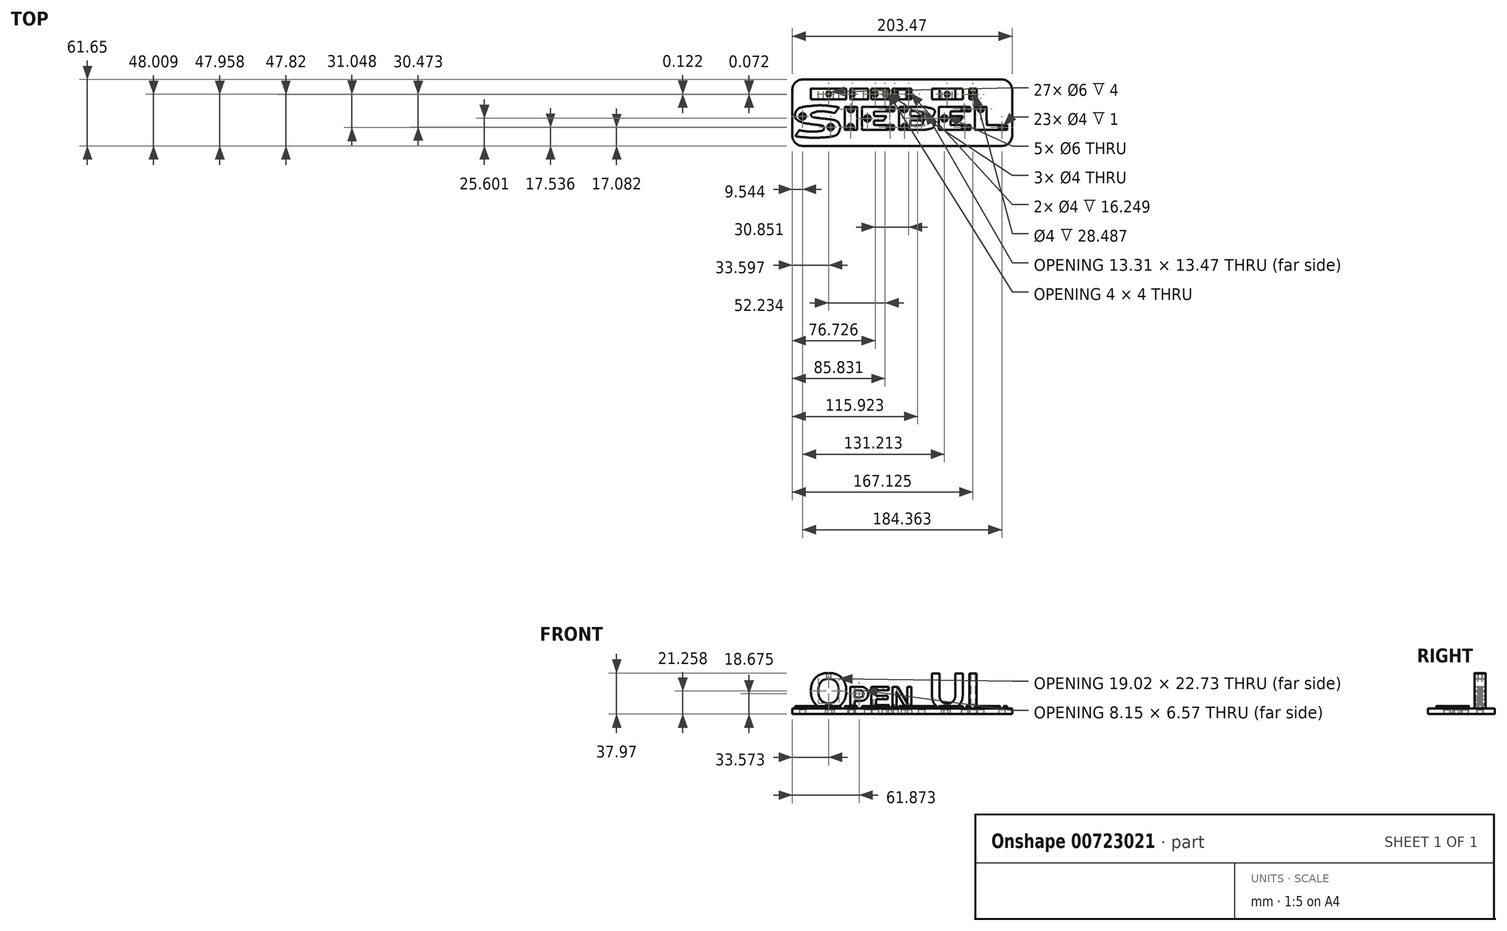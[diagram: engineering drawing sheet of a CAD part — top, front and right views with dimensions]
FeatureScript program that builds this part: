
annotation { "Feature Type Name" : "Feature", "Feature Type Description" : "" }
export const myFeature = defineFeature(function(context is Context, id is Id, definition is map)
    precondition{}
    {
        {
            var Q0;
            Q0=qCreatedBy(makeId("Top.planeOp"),FACE);
            var sketch = newSketch(context, id + "F0", { "sketchPlane" : qUnion([Q0])});
            skFitSpline(sketch, "E0", {"points": [v(-354.96, -59.06) * mm, v(-378.2, -57.21) * mm, v(-400.75, -54.4) * mm, v(-402.03, -53.2) * mm]});
            skFitSpline(sketch, "E1", {"points": [v(-402.03, -53.2) * mm, v(-402.4, -52.85) * mm, v(-399.54, -47.84) * mm, v(-395.68, -42.05) * mm]});
            skFitSpline(sketch, "E2", {"points": [v(-395.68, -42.05) * mm, v(-389.24, -32.38) * mm, v(-388.5, -31.56) * mm, v(-386.61, -31.95) * mm]});
            skFitSpline(sketch, "E3", {"points": [v(-386.61, -31.95) * mm, v(-370.93, -35.2) * mm, v(-331.08, -37.36) * mm, v(-318.28, -35.65) * mm]});
            skFitSpline(sketch, "E4", {"points": [v(-318.28, -35.65) * mm, v(-305.45, -33.93) * mm, v(-298.56, -29.94) * mm, v(-298.56, -24.22) * mm]});
            skFitSpline(sketch, "E5", {"points": [v(-298.56, -24.22) * mm, v(-298.56, -18.07) * mm, v(-306.97, -14.43) * mm, v(-327.76, -11.58) * mm]});
            skFitSpline(sketch, "E6", {"points": [v(-327.76, -11.58) * mm, v(-362.95, -6.76) * mm, v(-372.07, -5.05) * mm, v(-381.63, -1.45) * mm]});
            skFitSpline(sketch, "E7", {"points": [v(-381.63, -1.45) * mm, v(-389.44, 1.49) * mm, v(-392.84, 3.44) * mm, v(-397.15, 7.47) * mm]});
            skFitSpline(sketch, "E8", {"points": [v(-397.15, 7.47) * mm, v(-402.93, 12.88) * mm, v(-404.52, 16.34) * mm, v(-404.54, 23.62) * mm]});
            skFitSpline(sketch, "E9", {"points": [v(-404.54, 23.62) * mm, v(-404.56, 28.77) * mm, v(-404.24, 30.16) * mm, v(-402.32, 33.43) * mm]});
            skFitSpline(sketch, "E10", {"points": [v(-402.32, 33.43) * mm, v(-395.06, 45.78) * mm, v(-371.6, 54.87) * mm, v(-337.66, 58.48) * mm]});
            skFitSpline(sketch, "E11", {"points": [v(-337.66, 58.48) * mm, v(-322.85, 60.05) * mm, v(-292.3, 59.65) * mm, v(-275.36, 57.66) * mm]});
            skFitSpline(sketch, "E12", {"points": [v(-275.36, 57.66) * mm, v(-262.37, 56.14) * mm, v(-244.13, 53.26) * mm, v(-242.8, 52.53) * mm]});
            skFitSpline(sketch, "E13", {"points": [v(-242.8, 52.53) * mm, v(-242.17, 52.18) * mm, v(-244.56, 48.55) * mm, v(-249.77, 41.96) * mm]});
            skFitSpline(sketch, "E14", {"points": [v(-266.73, 33.28) * mm, v(-294.41, 37.46) * mm, v(-321.46, 37.5) * mm, v(-334.5, 33.4) * mm]});
            skFitSpline(sketch, "E15", {"points": [v(-334.5, 33.4) * mm, v(-342.06, 31.02) * mm, v(-345.84, 25.86) * mm, v(-343.4, 21.28) * mm]});
            skFitSpline(sketch, "E16", {"points": [v(-343.4, 21.28) * mm, v(-341.53, 17.8) * mm, v(-331.4, 15.1) * mm, v(-310.06, 12.42) * mm]});
            skFitSpline(sketch, "E17", {"points": [v(-310.06, 12.42) * mm, v(-266.73, 6.98) * mm, v(-246.51, -0.28) * mm, v(-239.92, -12.73) * mm]});
            skFitSpline(sketch, "E18", {"points": [v(-239.92, -12.73) * mm, v(-237.55, -17.2) * mm, v(-237.58, -25.67) * mm, v(-239.99, -31.03) * mm]});
            skFitSpline(sketch, "E19", {"points": [v(-239.99, -31.03) * mm, v(-246.48, -45.5) * mm, v(-271.26, -55.64) * mm, v(-307.76, -58.75) * mm]});
            skFitSpline(sketch, "E20", {"points": [v(-307.76, -58.75) * mm, v(-316.45, -59.49) * mm, v(-347.03, -59.7) * mm, v(-354.96, -59.06) * mm]});
            skLineSegment(sketch, "E21", {"start": v(-249.77, 41.96) * mm, "end": v(-257.7, 31.91) * mm});
            skLineSegment(sketch, "E22", {"start": v(-257.7, 31.91) * mm, "end": v(-266.73, 33.28) * mm});
            skLineSegment(sketch, "E23", {"start": v(-220.96, 12.02) * mm, "end": v(-220.96, 54.82) * mm});
            skLineSegment(sketch, "E24", {"start": v(-220.96, 54.82) * mm, "end": v(-197.76, 54.82) * mm});
            skLineSegment(sketch, "E25", {"start": v(-197.76, 54.82) * mm, "end": v(-174.56, 54.82) * mm});
            skLineSegment(sketch, "E26", {"start": v(-174.56, 54.82) * mm, "end": v(-174.56, 12.02) * mm});
            skLineSegment(sketch, "E27", {"start": v(-174.56, 12.02) * mm, "end": v(-174.56, -30.78) * mm});
            skLineSegment(sketch, "E28", {"start": v(-174.56, -30.78) * mm, "end": v(-197.76, -30.78) * mm});
            skLineSegment(sketch, "E29", {"start": v(-197.76, -30.78) * mm, "end": v(-220.96, -30.78) * mm});
            skLineSegment(sketch, "E30", {"start": v(-220.96, -30.78) * mm, "end": v(-220.96, 12.02) * mm});
            skFitSpline(sketch, "E31", {"points": [v(-20.16, 1.76) * mm, v(-20.16, 19.72) * mm, v(-19.92, 39) * mm, v(-19.63, 44.62) * mm]});
            skLineSegment(sketch, "E32", {"start": v(-156.96, 12.02) * mm, "end": v(-156.96, 54.82) * mm});
            skLineSegment(sketch, "E33", {"start": v(-156.96, 54.82) * mm, "end": v(-96.93, 54.82) * mm});
            skLineSegment(sketch, "E34", {"start": v(-96.93, 54.82) * mm, "end": v(-36.9, 54.82) * mm});
            skLineSegment(sketch, "E35", {"start": v(-36.9, 54.82) * mm, "end": v(-37.13, 46.22) * mm});
            skLineSegment(sketch, "E36", {"start": v(-37.13, 46.22) * mm, "end": v(-37.36, 37.62) * mm});
            skLineSegment(sketch, "E37", {"start": v(-37.36, 37.62) * mm, "end": v(-74.79, 37.4) * mm});
            skLineSegment(sketch, "E38", {"start": v(-74.79, 37.4) * mm, "end": v(-112.22, 37.2) * mm});
            skLineSegment(sketch, "E39", {"start": v(-112.22, 37.2) * mm, "end": v(-111.99, 29) * mm});
            skLineSegment(sketch, "E40", {"start": v(-111.99, 29) * mm, "end": v(-111.76, 20.82) * mm});
            skLineSegment(sketch, "E41", {"start": v(-111.76, 20.82) * mm, "end": v(-89.19, 20.42) * mm});
            skLineSegment(sketch, "E42", {"start": v(-89.19, 20.42) * mm, "end": v(-66.62, 20.02) * mm});
            skLineSegment(sketch, "E43", {"start": v(-66.62, 20.02) * mm, "end": v(-71.86, 11.82) * mm});
            skLineSegment(sketch, "E44", {"start": v(-71.86, 11.82) * mm, "end": v(-77.1, 3.62) * mm});
            skLineSegment(sketch, "E45", {"start": v(-77.1, 3.62) * mm, "end": v(-94.63, 3.62) * mm});
            skLineSegment(sketch, "E46", {"start": v(-94.63, 3.62) * mm, "end": v(-112.16, 3.62) * mm});
            skLineSegment(sketch, "E47", {"start": v(-112.16, 3.62) * mm, "end": v(-112.16, -4.78) * mm});
            skLineSegment(sketch, "E48", {"start": v(-112.16, -4.78) * mm, "end": v(-112.16, -13.18) * mm});
            skLineSegment(sketch, "E49", {"start": v(-112.16, -13.18) * mm, "end": v(-75.36, -13.18) * mm});
            skLineSegment(sketch, "E50", {"start": v(-75.36, -13.18) * mm, "end": v(-38.56, -13.18) * mm});
            skLineSegment(sketch, "E51", {"start": v(-38.56, -13.18) * mm, "end": v(-38.56, -21.98) * mm});
            skLineSegment(sketch, "E52", {"start": v(-38.56, -21.98) * mm, "end": v(-38.56, -30.78) * mm});
            skLineSegment(sketch, "E53", {"start": v(-38.56, -30.78) * mm, "end": v(-97.76, -30.78) * mm});
            skLineSegment(sketch, "E54", {"start": v(-97.76, -30.78) * mm, "end": v(-156.96, -30.78) * mm});
            skLineSegment(sketch, "E55", {"start": v(-156.96, -30.78) * mm, "end": v(-156.96, 12.02) * mm});
            skFitSpline(sketch, "E56", {"points": [v(24.16, 54.8) * mm, v(68.81, 54.78) * mm, v(77.5, 54.3) * mm, v(89.34, 51.24) * mm]});
            skFitSpline(sketch, "E57", {"points": [v(89.34, 51.24) * mm, v(105.78, 46.98) * mm, v(113.7, 38.02) * mm, v(109.88, 28.02) * mm]});
            skFitSpline(sketch, "E58", {"points": [v(109.88, 28.02) * mm, v(107.47, 21.7) * mm, v(100.41, 17.1) * mm, v(88.56, 14.12) * mm]});
            skFitSpline(sketch, "E59", {"points": [v(88.56, 14.12) * mm, v(83.93, 12.95) * mm, v(83.08, 12.52) * mm, v(84.64, 12.17) * mm]});
            skFitSpline(sketch, "E60", {"points": [v(84.64, 12.17) * mm, v(95.63, 9.67) * mm, v(98.47, 8.79) * mm, v(102.58, 6.57) * mm]});
            skFitSpline(sketch, "E61", {"points": [v(102.58, 6.57) * mm, v(109.46, 2.87) * mm, v(112.1, -0.78) * mm, v(112.44, -7.01) * mm]});
            skFitSpline(sketch, "E62", {"points": [v(112.44, -7.01) * mm, v(112.66, -11.07) * mm, v(112.37, -12.57) * mm, v(110.86, -15.16) * mm]});
            skFitSpline(sketch, "E63", {"points": [v(110.86, -15.16) * mm, v(107.2, -21.45) * mm, v(98.2, -25.98) * mm, v(83.44, -28.93) * mm]});
            skFitSpline(sketch, "E64", {"points": [v(83.44, -28.93) * mm, v(78.12, -30) * mm, v(68.82, -30.27) * mm, v(28.44, -30.55) * mm]});
            skLineSegment(sketch, "E65", {"start": v(-19.63, 44.62) * mm, "end": v(-19.11, 54.82) * mm});
            skLineSegment(sketch, "E66", {"start": v(-19.11, 54.82) * mm, "end": v(24.16, 54.8) * mm});
            skFitSpline(sketch, "E67", {"points": [v(62.24, -12.7) * mm, v(66.78, -10.61) * mm, v(68.16, -8.94) * mm, v(68.16, -5.53) * mm]});
            skFitSpline(sketch, "E68", {"points": [v(68.16, -5.53) * mm, v(68.16, -2.08) * mm, v(65.6, 0.7) * mm, v(60.74, 2.52) * mm]});
            skFitSpline(sketch, "E69", {"points": [v(60.74, 2.52) * mm, v(57.78, 3.63) * mm, v(53.58, 3.96) * mm, v(39.64, 4.23) * mm]});
            skLineSegment(sketch, "E70", {"start": v(28.44, -30.55) * mm, "end": v(-20.16, -30.9) * mm});
            skLineSegment(sketch, "E71", {"start": v(-20.16, -30.9) * mm, "end": v(-20.16, 1.76) * mm});
            skLineSegment(sketch, "E72", {"start": v(-20.16, 1.76) * mm, "end": v(-20.16, 1.76) * mm});
            skFitSpline(sketch, "E73", {"points": [v(40.44, -14.64) * mm, v(56.77, -14.38) * mm, v(59.01, -14.18) * mm, v(62.24, -12.7) * mm]});
            skLineSegment(sketch, "E74", {"start": v(39.64, 4.23) * mm, "end": v(22.24, 4.55) * mm});
            skLineSegment(sketch, "E75", {"start": v(22.24, 4.55) * mm, "end": v(22.24, -5.2) * mm});
            skLineSegment(sketch, "E76", {"start": v(22.24, -5.2) * mm, "end": v(22.24, -14.94) * mm});
            skLineSegment(sketch, "E77", {"start": v(22.24, -14.94) * mm, "end": v(40.44, -14.64) * mm});
            skFitSpline(sketch, "E78", {"points": [v(55.04, 21.27) * mm, v(57.9, 21.74) * mm, v(61.67, 22.9) * mm, v(63.42, 23.87) * mm]});
            skFitSpline(sketch, "E79", {"points": [v(63.42, 23.87) * mm, v(69.57, 27.26) * mm, v(69.07, 33.28) * mm, v(62.36, 36.59) * mm]});
            skFitSpline(sketch, "E80", {"points": [v(62.36, 36.59) * mm, v(58.87, 38.3) * mm, v(57.5, 38.43) * mm, v(40.44, 38.68) * mm]});
            skFitSpline(sketch, "E81", {"points": [v(36.04, 20.42) * mm, v(43.63, 20.43) * mm, v(52.18, 20.8) * mm, v(55.04, 21.27) * mm]});
            skLineSegment(sketch, "E82", {"start": v(40.44, 38.68) * mm, "end": v(22.24, 38.95) * mm});
            skLineSegment(sketch, "E83", {"start": v(22.24, 38.95) * mm, "end": v(22.24, 29.68) * mm});
            skLineSegment(sketch, "E84", {"start": v(22.24, 29.68) * mm, "end": v(22.24, 20.42) * mm});
            skLineSegment(sketch, "E85", {"start": v(22.24, 20.42) * mm, "end": v(36.04, 20.42) * mm});
            skLineSegment(sketch, "E86", {"start": v(55.04, 21.27) * mm, "end": v(55.04, 21.27) * mm});
            skFitSpline(sketch, "E87", {"points": [v(243.32, 48.7) * mm, v(243.6, 45.33) * mm, v(243.84, 41.55) * mm, v(243.84, 40.3) * mm]});
            skLineSegment(sketch, "E88", {"start": v(127.04, 12.02) * mm, "end": v(127.04, 54.82) * mm});
            skLineSegment(sketch, "E89", {"start": v(127.04, 54.82) * mm, "end": v(184.92, 54.82) * mm});
            skLineSegment(sketch, "E90", {"start": v(184.92, 54.82) * mm, "end": v(242.8, 54.82) * mm});
            skLineSegment(sketch, "E91", {"start": v(242.8, 54.82) * mm, "end": v(243.32, 48.7) * mm});
            skLineSegment(sketch, "E92", {"start": v(243.84, 40.3) * mm, "end": v(243.84, 38.02) * mm});
            skLineSegment(sketch, "E93", {"start": v(243.84, 38.02) * mm, "end": v(207.44, 38.02) * mm});
            skLineSegment(sketch, "E94", {"start": v(207.44, 38.02) * mm, "end": v(171.04, 38.02) * mm});
            skLineSegment(sketch, "E95", {"start": v(171.04, 38.02) * mm, "end": v(171.04, 29.23) * mm});
            skLineSegment(sketch, "E96", {"start": v(171.04, 29.23) * mm, "end": v(171.04, 20.44) * mm});
            skLineSegment(sketch, "E97", {"start": v(171.04, 20.44) * mm, "end": v(193.73, 20.23) * mm});
            skLineSegment(sketch, "E98", {"start": v(193.73, 20.23) * mm, "end": v(216.43, 20.02) * mm});
            skLineSegment(sketch, "E99", {"start": v(216.43, 20.02) * mm, "end": v(211.18, 11.82) * mm});
            skLineSegment(sketch, "E100", {"start": v(211.18, 11.82) * mm, "end": v(205.94, 3.62) * mm});
            skLineSegment(sketch, "E101", {"start": v(205.94, 3.62) * mm, "end": v(188.49, 3.62) * mm});
            skLineSegment(sketch, "E102", {"start": v(188.49, 3.62) * mm, "end": v(171.04, 3.62) * mm});
            skLineSegment(sketch, "E103", {"start": v(171.04, 3.62) * mm, "end": v(171.04, -4.78) * mm});
            skLineSegment(sketch, "E104", {"start": v(171.04, -4.78) * mm, "end": v(171.04, -13.18) * mm});
            skLineSegment(sketch, "E105", {"start": v(171.04, -13.18) * mm, "end": v(207.44, -13.18) * mm});
            skLineSegment(sketch, "E106", {"start": v(207.44, -13.18) * mm, "end": v(243.84, -13.18) * mm});
            skLineSegment(sketch, "E107", {"start": v(243.84, -13.18) * mm, "end": v(243.84, -21.98) * mm});
            skLineSegment(sketch, "E108", {"start": v(243.84, -21.98) * mm, "end": v(243.84, -30.78) * mm});
            skLineSegment(sketch, "E109", {"start": v(243.84, -30.78) * mm, "end": v(185.44, -30.78) * mm});
            skLineSegment(sketch, "E110", {"start": v(185.44, -30.78) * mm, "end": v(127.04, -30.78) * mm});
            skLineSegment(sketch, "E111", {"start": v(127.04, -30.78) * mm, "end": v(127.04, 12.02) * mm});
            skFitSpline(sketch, "E112", {"points": [v(304.64, 30.22) * mm, v(304.65, 16.69) * mm, v(304.88, 1.57) * mm, v(305.17, -3.38) * mm]});
            skLineSegment(sketch, "E113", {"start": v(260.64, 12.02) * mm, "end": v(260.64, 54.82) * mm});
            skLineSegment(sketch, "E114", {"start": v(260.64, 54.82) * mm, "end": v(282.64, 54.82) * mm});
            skLineSegment(sketch, "E115", {"start": v(282.64, 54.82) * mm, "end": v(304.64, 54.82) * mm});
            skLineSegment(sketch, "E116", {"start": v(304.64, 54.82) * mm, "end": v(304.64, 30.22) * mm});
            skLineSegment(sketch, "E117", {"start": v(305.17, -3.38) * mm, "end": v(305.68, -12.38) * mm});
            skLineSegment(sketch, "E118", {"start": v(305.68, -12.38) * mm, "end": v(343.16, -12.38) * mm});
            skLineSegment(sketch, "E119", {"start": v(343.16, -12.38) * mm, "end": v(380.64, -12.38) * mm});
            skLineSegment(sketch, "E120", {"start": v(380.64, -12.38) * mm, "end": v(380.64, -21.58) * mm});
            skLineSegment(sketch, "E121", {"start": v(380.64, -21.58) * mm, "end": v(380.64, -30.78) * mm});
            skLineSegment(sketch, "E122", {"start": v(380.64, -30.78) * mm, "end": v(320.64, -30.78) * mm});
            skLineSegment(sketch, "E123", {"start": v(320.64, -30.78) * mm, "end": v(260.64, -30.78) * mm});
            skLineSegment(sketch, "E124", {"start": v(260.64, -30.78) * mm, "end": v(260.64, 12.02) * mm});
            skSolve(sketch);
        }
        {
            var Q0;
            Q0=makeQuery(id+"F0.imprint","IMPRINT",FACE,{"disambiguationData":[TD([[makeQuery(id+"F0.imprint","IMPRINT",EDGE,{"derivedFrom":sQuery(id+"F0.wireOp",EDGE,"E0")}),-1.0]])]});
            var Q1;
            Q1=makeQuery(id+"F0.imprint","IMPRINT",FACE,{"disambiguationData":[TD([[makeQuery(id+"F0.imprint","IMPRINT",EDGE,{"derivedFrom":sQuery(id+"F0.wireOp",EDGE,"E23")}),-1.0]])]});
            var Q2;
            Q2=makeQuery(id+"F0.imprint","IMPRINT",FACE,{"disambiguationData":[TD([[makeQuery(id+"F0.imprint","IMPRINT",EDGE,{"derivedFrom":sQuery(id+"F0.wireOp",EDGE,"E32")}),-1.0]])]});
            var Q3;
            Q3=makeQuery(id+"F0.imprint","IMPRINT",FACE,{"disambiguationData":[TD([[makeQuery(id+"F0.imprint","IMPRINT",EDGE,{"derivedFrom":sQuery(id+"F0.wireOp",EDGE,"E31")}),-1.0]])]});
            var Q4;
            Q4=makeQuery(id+"F0.imprint","IMPRINT",FACE,{"disambiguationData":[TD([[makeQuery(id+"F0.imprint","IMPRINT",EDGE,{"derivedFrom":sQuery(id+"F0.wireOp",EDGE,"E87")}),-1.0]])]});
            var Q5;
            Q5=makeQuery(id+"F0.imprint","IMPRINT",FACE,{"disambiguationData":[TD([[makeQuery(id+"F0.imprint","IMPRINT",EDGE,{"derivedFrom":sQuery(id+"F0.wireOp",EDGE,"E112")}),-1.0]])]});
            extrude(context, id + "F1", {"entities" : qUnion([Q0, Q1, Q2, Q3, Q4, Q5]), "depth" : 10 * mm, "offsetDistance" : 25 * mm});
        }
        {
            var Q0;
            Q0=qCreatedBy(makeId("Front.planeOp"),FACE);
            var sketch = newSketch(context, id + "F2", { "sketchPlane" : qUnion([Q0])});
            skText(sketch, "E125", { "text": "UI", "fontName": "Arimo-Bold.ttf"});
            skText(sketch, "E126", { "text": "O", "fontName": "Arimo-Bold.ttf"});
            skText(sketch, "E127", { "text": "PEN", "fontName": "Arimo-Bold.ttf"});
            const initialGuessF2  = {"E125": [-0.03631, 0, 1, 0, 0.085], "E126": [-0.31434, 0, 1, 0, 0.085], "E127": [-0.22355, 0, 1, 0, 0.05298]};
            skSetInitialGuess(sketch, initialGuessF2);
            skSolve(sketch);
        }
        {
            var Q0;
            Q0 = qSketchRegion(id + "F2", true);
            extrude(context, id + "F3", {"entities" : qUnion([Q0]), "depth" : 25 * mm, "offsetDistance" : 25 * mm});
        }
        {
            var Q0;
            Q0=makeQuery(id+"F3.opExtrude","SWEPT_BODY",BODY,{"disambiguationData":[OSD([sQuery(id+"F2.wireOp",EDGE,"E127.sketch_text.stroke-28"),sQuery(id+"F2.wireOp",EDGE,"E127.sketch_text.stroke-29"),sQuery(id+"F2.wireOp",EDGE,"E127.sketch_text.stroke-30"),sQuery(id+"F2.wireOp",EDGE,"E127.sketch_text.stroke-31"),sQuery(id+"F2.wireOp",EDGE,"E127.sketch_text.stroke-32"),sQuery(id+"F2.wireOp",EDGE,"E127.sketch_text.stroke-33"),sQuery(id+"F2.wireOp",EDGE,"E127.sketch_text.stroke-34"),sQuery(id+"F2.wireOp",EDGE,"E127.sketch_text.stroke-35"),sQuery(id+"F2.wireOp",EDGE,"E127.sketch_text.stroke-36"),sQuery(id+"F2.wireOp",EDGE,"E127.sketch_text.stroke-37"),sQuery(id+"F2.wireOp",EDGE,"E127.sketch_text.stroke-38"),sQuery(id+"F2.wireOp",EDGE,"E127.sketch_text.stroke-39")])]});
            var Q1;
            Q1=makeQuery(id+"F3.opExtrude","SWEPT_BODY",BODY,{"disambiguationData":[OSD([sQuery(id+"F2.wireOp",EDGE,"E127.sketch_text.stroke-16"),sQuery(id+"F2.wireOp",EDGE,"E127.sketch_text.stroke-17"),sQuery(id+"F2.wireOp",EDGE,"E127.sketch_text.stroke-18"),sQuery(id+"F2.wireOp",EDGE,"E127.sketch_text.stroke-19"),sQuery(id+"F2.wireOp",EDGE,"E127.sketch_text.stroke-20"),sQuery(id+"F2.wireOp",EDGE,"E127.sketch_text.stroke-21"),sQuery(id+"F2.wireOp",EDGE,"E127.sketch_text.stroke-22"),sQuery(id+"F2.wireOp",EDGE,"E127.sketch_text.stroke-23"),sQuery(id+"F2.wireOp",EDGE,"E127.sketch_text.stroke-24"),sQuery(id+"F2.wireOp",EDGE,"E127.sketch_text.stroke-25"),sQuery(id+"F2.wireOp",EDGE,"E127.sketch_text.stroke-26"),sQuery(id+"F2.wireOp",EDGE,"E127.sketch_text.stroke-27")])]});
            var Q2;
            Q2=makeQuery(id+"F3.opExtrude","SWEPT_BODY",BODY,{"disambiguationData":[OSD([sQuery(id+"F2.wireOp",EDGE,"E127.sketch_text.stroke-0"),sQuery(id+"F2.wireOp",EDGE,"E127.sketch_text.stroke-1"),sQuery(id+"F2.wireOp",EDGE,"E127.sketch_text.stroke-2"),sQuery(id+"F2.wireOp",EDGE,"E127.sketch_text.stroke-3"),sQuery(id+"F2.wireOp",EDGE,"E127.sketch_text.stroke-4"),sQuery(id+"F2.wireOp",EDGE,"E127.sketch_text.stroke-5"),sQuery(id+"F2.wireOp",EDGE,"E127.sketch_text.stroke-6"),sQuery(id+"F2.wireOp",EDGE,"E127.sketch_text.stroke-7"),sQuery(id+"F2.wireOp",EDGE,"E127.sketch_text.stroke-8"),sQuery(id+"F2.wireOp",EDGE,"E127.sketch_text.stroke-9"),sQuery(id+"F2.wireOp",EDGE,"E127.sketch_text.stroke-10"),sQuery(id+"F2.wireOp",EDGE,"E127.sketch_text.stroke-11"),sQuery(id+"F2.wireOp",EDGE,"E127.sketch_text.stroke-12"),sQuery(id+"F2.wireOp",EDGE,"E127.sketch_text.stroke-13"),sQuery(id+"F2.wireOp",EDGE,"E127.sketch_text.stroke-14"),sQuery(id+"F2.wireOp",EDGE,"E127.sketch_text.stroke-15")])]});
            var Q3;
            Q3=makeQuery(id+"F3.opExtrude","SWEPT_BODY",BODY,{"disambiguationData":[OSD([sQuery(id+"F2.wireOp",EDGE,"E126.sketch_text.stroke-0"),sQuery(id+"F2.wireOp",EDGE,"E126.sketch_text.stroke-1"),sQuery(id+"F2.wireOp",EDGE,"E126.sketch_text.stroke-2"),sQuery(id+"F2.wireOp",EDGE,"E126.sketch_text.stroke-3"),sQuery(id+"F2.wireOp",EDGE,"E126.sketch_text.stroke-4"),sQuery(id+"F2.wireOp",EDGE,"E126.sketch_text.stroke-5"),sQuery(id+"F2.wireOp",EDGE,"E126.sketch_text.stroke-6"),sQuery(id+"F2.wireOp",EDGE,"E126.sketch_text.stroke-7"),sQuery(id+"F2.wireOp",EDGE,"E126.sketch_text.stroke-8"),sQuery(id+"F2.wireOp",EDGE,"E126.sketch_text.stroke-9"),sQuery(id+"F2.wireOp",EDGE,"E126.sketch_text.stroke-10"),sQuery(id+"F2.wireOp",EDGE,"E126.sketch_text.stroke-11"),sQuery(id+"F2.wireOp",EDGE,"E126.sketch_text.stroke-12"),sQuery(id+"F2.wireOp",EDGE,"E126.sketch_text.stroke-13"),sQuery(id+"F2.wireOp",EDGE,"E126.sketch_text.stroke-14"),sQuery(id+"F2.wireOp",EDGE,"E126.sketch_text.stroke-15"),sQuery(id+"F2.wireOp",EDGE,"E126.sketch_text.stroke-16")])]});
            var Q4;
            Q4=makeQuery(id+"F3.opExtrude","SWEPT_BODY",BODY,{"disambiguationData":[OSD([sQuery(id+"F2.wireOp",EDGE,"E125.sketch_text.stroke-14"),sQuery(id+"F2.wireOp",EDGE,"E125.sketch_text.stroke-15"),sQuery(id+"F2.wireOp",EDGE,"E125.sketch_text.stroke-16"),sQuery(id+"F2.wireOp",EDGE,"E125.sketch_text.stroke-17")])]});
            var Q5;
            Q5=makeQuery(id+"F3.opExtrude","SWEPT_BODY",BODY,{"disambiguationData":[OSD([sQuery(id+"F2.wireOp",EDGE,"E125.sketch_text.stroke-0"),sQuery(id+"F2.wireOp",EDGE,"E125.sketch_text.stroke-1"),sQuery(id+"F2.wireOp",EDGE,"E125.sketch_text.stroke-2"),sQuery(id+"F2.wireOp",EDGE,"E125.sketch_text.stroke-3"),sQuery(id+"F2.wireOp",EDGE,"E125.sketch_text.stroke-4"),sQuery(id+"F2.wireOp",EDGE,"E125.sketch_text.stroke-5"),sQuery(id+"F2.wireOp",EDGE,"E125.sketch_text.stroke-6"),sQuery(id+"F2.wireOp",EDGE,"E125.sketch_text.stroke-7"),sQuery(id+"F2.wireOp",EDGE,"E125.sketch_text.stroke-8"),sQuery(id+"F2.wireOp",EDGE,"E125.sketch_text.stroke-9"),sQuery(id+"F2.wireOp",EDGE,"E125.sketch_text.stroke-10"),sQuery(id+"F2.wireOp",EDGE,"E125.sketch_text.stroke-11"),sQuery(id+"F2.wireOp",EDGE,"E125.sketch_text.stroke-12"),sQuery(id+"F2.wireOp",EDGE,"E125.sketch_text.stroke-13")])]});
            transform(context, id + "F4", {"entities" : qUnion([Q0, Q1, Q2, Q3, Q4, Q5]), "transformType" : TransformType.TRANSLATION_3D, "dx" : 0 * mm, "dy" : 107 * mm, "dz" : 0 * mm, "makeCopy" : false});
        }
        {
            var Q0;
            Q0=makeQuery(id+"F1.opExtrude","SWEPT_BODY",BODY,{"disambiguationData":[OSD([sQuery(id+"F0.wireOp",EDGE,"E0"),sQuery(id+"F0.wireOp",EDGE,"E1"),sQuery(id+"F0.wireOp",EDGE,"E2"),sQuery(id+"F0.wireOp",EDGE,"E3"),sQuery(id+"F0.wireOp",EDGE,"E4"),sQuery(id+"F0.wireOp",EDGE,"E5"),sQuery(id+"F0.wireOp",EDGE,"E6"),sQuery(id+"F0.wireOp",EDGE,"E7"),sQuery(id+"F0.wireOp",EDGE,"E8"),sQuery(id+"F0.wireOp",EDGE,"E9"),sQuery(id+"F0.wireOp",EDGE,"E10"),sQuery(id+"F0.wireOp",EDGE,"E11"),sQuery(id+"F0.wireOp",EDGE,"E12"),sQuery(id+"F0.wireOp",EDGE,"E13"),sQuery(id+"F0.wireOp",EDGE,"E14"),sQuery(id+"F0.wireOp",EDGE,"E15"),sQuery(id+"F0.wireOp",EDGE,"E16"),sQuery(id+"F0.wireOp",EDGE,"E17"),sQuery(id+"F0.wireOp",EDGE,"E18"),sQuery(id+"F0.wireOp",EDGE,"E19"),sQuery(id+"F0.wireOp",EDGE,"E20"),sQuery(id+"F0.wireOp",EDGE,"E21"),sQuery(id+"F0.wireOp",EDGE,"E22")])]});
            var Q1;
            Q1=makeQuery(id+"F1.opExtrude","SWEPT_BODY",BODY,{"disambiguationData":[OSD([sQuery(id+"F0.wireOp",EDGE,"E112"),sQuery(id+"F0.wireOp",EDGE,"E113"),sQuery(id+"F0.wireOp",EDGE,"E114"),sQuery(id+"F0.wireOp",EDGE,"E115"),sQuery(id+"F0.wireOp",EDGE,"E116"),sQuery(id+"F0.wireOp",EDGE,"E117"),sQuery(id+"F0.wireOp",EDGE,"E118"),sQuery(id+"F0.wireOp",EDGE,"E119"),sQuery(id+"F0.wireOp",EDGE,"E120"),sQuery(id+"F0.wireOp",EDGE,"E121"),sQuery(id+"F0.wireOp",EDGE,"E122"),sQuery(id+"F0.wireOp",EDGE,"E123"),sQuery(id+"F0.wireOp",EDGE,"E124")])]});
            var Q2;
            Q2=makeQuery(id+"F1.opExtrude","SWEPT_BODY",BODY,{"disambiguationData":[OSD([sQuery(id+"F0.wireOp",EDGE,"E23"),sQuery(id+"F0.wireOp",EDGE,"E24"),sQuery(id+"F0.wireOp",EDGE,"E25"),sQuery(id+"F0.wireOp",EDGE,"E26"),sQuery(id+"F0.wireOp",EDGE,"E27"),sQuery(id+"F0.wireOp",EDGE,"E28"),sQuery(id+"F0.wireOp",EDGE,"E29"),sQuery(id+"F0.wireOp",EDGE,"E30")])]});
            var Q3;
            Q3=makeQuery(id+"F1.opExtrude","SWEPT_BODY",BODY,{"disambiguationData":[OSD([sQuery(id+"F0.wireOp",EDGE,"E31"),sQuery(id+"F0.wireOp",EDGE,"E56"),sQuery(id+"F0.wireOp",EDGE,"E57"),sQuery(id+"F0.wireOp",EDGE,"E58"),sQuery(id+"F0.wireOp",EDGE,"E59"),sQuery(id+"F0.wireOp",EDGE,"E60"),sQuery(id+"F0.wireOp",EDGE,"E61"),sQuery(id+"F0.wireOp",EDGE,"E62"),sQuery(id+"F0.wireOp",EDGE,"E63"),sQuery(id+"F0.wireOp",EDGE,"E64"),sQuery(id+"F0.wireOp",EDGE,"E65"),sQuery(id+"F0.wireOp",EDGE,"E66"),sQuery(id+"F0.wireOp",EDGE,"E67"),sQuery(id+"F0.wireOp",EDGE,"E68"),sQuery(id+"F0.wireOp",EDGE,"E69"),sQuery(id+"F0.wireOp",EDGE,"E70"),sQuery(id+"F0.wireOp",EDGE,"E71"),sQuery(id+"F0.wireOp",EDGE,"E73"),sQuery(id+"F0.wireOp",EDGE,"E74"),sQuery(id+"F0.wireOp",EDGE,"E75"),sQuery(id+"F0.wireOp",EDGE,"E76"),sQuery(id+"F0.wireOp",EDGE,"E77"),sQuery(id+"F0.wireOp",EDGE,"E78"),sQuery(id+"F0.wireOp",EDGE,"E79"),sQuery(id+"F0.wireOp",EDGE,"E80"),sQuery(id+"F0.wireOp",EDGE,"E81"),sQuery(id+"F0.wireOp",EDGE,"E82"),sQuery(id+"F0.wireOp",EDGE,"E83"),sQuery(id+"F0.wireOp",EDGE,"E84"),sQuery(id+"F0.wireOp",EDGE,"E85"),sQuery(id+"F0.wireOp",EDGE,"E86")])]});
            var Q4;
            Q4=makeQuery(id+"F1.opExtrude","SWEPT_BODY",BODY,{"disambiguationData":[OSD([sQuery(id+"F0.wireOp",EDGE,"E32"),sQuery(id+"F0.wireOp",EDGE,"E33"),sQuery(id+"F0.wireOp",EDGE,"E34"),sQuery(id+"F0.wireOp",EDGE,"E35"),sQuery(id+"F0.wireOp",EDGE,"E36"),sQuery(id+"F0.wireOp",EDGE,"E37"),sQuery(id+"F0.wireOp",EDGE,"E38"),sQuery(id+"F0.wireOp",EDGE,"E39"),sQuery(id+"F0.wireOp",EDGE,"E40"),sQuery(id+"F0.wireOp",EDGE,"E41"),sQuery(id+"F0.wireOp",EDGE,"E42"),sQuery(id+"F0.wireOp",EDGE,"E43"),sQuery(id+"F0.wireOp",EDGE,"E44"),sQuery(id+"F0.wireOp",EDGE,"E45"),sQuery(id+"F0.wireOp",EDGE,"E46"),sQuery(id+"F0.wireOp",EDGE,"E47"),sQuery(id+"F0.wireOp",EDGE,"E48"),sQuery(id+"F0.wireOp",EDGE,"E49"),sQuery(id+"F0.wireOp",EDGE,"E50"),sQuery(id+"F0.wireOp",EDGE,"E51"),sQuery(id+"F0.wireOp",EDGE,"E52"),sQuery(id+"F0.wireOp",EDGE,"E53"),sQuery(id+"F0.wireOp",EDGE,"E54"),sQuery(id+"F0.wireOp",EDGE,"E55")])]});
            var Q5;
            Q5=makeQuery(id+"F1.opExtrude","SWEPT_BODY",BODY,{"disambiguationData":[OSD([sQuery(id+"F0.wireOp",EDGE,"E87"),sQuery(id+"F0.wireOp",EDGE,"E88"),sQuery(id+"F0.wireOp",EDGE,"E89"),sQuery(id+"F0.wireOp",EDGE,"E90"),sQuery(id+"F0.wireOp",EDGE,"E91"),sQuery(id+"F0.wireOp",EDGE,"E92"),sQuery(id+"F0.wireOp",EDGE,"E93"),sQuery(id+"F0.wireOp",EDGE,"E94"),sQuery(id+"F0.wireOp",EDGE,"E95"),sQuery(id+"F0.wireOp",EDGE,"E96"),sQuery(id+"F0.wireOp",EDGE,"E97"),sQuery(id+"F0.wireOp",EDGE,"E98"),sQuery(id+"F0.wireOp",EDGE,"E99"),sQuery(id+"F0.wireOp",EDGE,"E100"),sQuery(id+"F0.wireOp",EDGE,"E101"),sQuery(id+"F0.wireOp",EDGE,"E102"),sQuery(id+"F0.wireOp",EDGE,"E103"),sQuery(id+"F0.wireOp",EDGE,"E104"),sQuery(id+"F0.wireOp",EDGE,"E105"),sQuery(id+"F0.wireOp",EDGE,"E106"),sQuery(id+"F0.wireOp",EDGE,"E107"),sQuery(id+"F0.wireOp",EDGE,"E108"),sQuery(id+"F0.wireOp",EDGE,"E109"),sQuery(id+"F0.wireOp",EDGE,"E110"),sQuery(id+"F0.wireOp",EDGE,"E111")])]});
            var Q6;
            Q6=qCreatedBy(makeId("Origin.pointOp"),VERTEX);
            transform(context, id + "F5", {"entities" : qUnion([Q0, Q1, Q2, Q3, Q4, Q5]), "transformType" : TransformType.SCALE_UNIFORMLY, "scale" : 0.25, "scalePoint" : qUnion([Q6]), "makeCopy" : false});
        }
        {
            var Q0;
            Q0=makeQuery(id+"F3.opExtrude","SWEPT_BODY",BODY,{"disambiguationData":[OSD([sQuery(id+"F2.wireOp",EDGE,"E125.sketch_text.stroke-0"),sQuery(id+"F2.wireOp",EDGE,"E125.sketch_text.stroke-1"),sQuery(id+"F2.wireOp",EDGE,"E125.sketch_text.stroke-2"),sQuery(id+"F2.wireOp",EDGE,"E125.sketch_text.stroke-3"),sQuery(id+"F2.wireOp",EDGE,"E125.sketch_text.stroke-4"),sQuery(id+"F2.wireOp",EDGE,"E125.sketch_text.stroke-5"),sQuery(id+"F2.wireOp",EDGE,"E125.sketch_text.stroke-6"),sQuery(id+"F2.wireOp",EDGE,"E125.sketch_text.stroke-7"),sQuery(id+"F2.wireOp",EDGE,"E125.sketch_text.stroke-8"),sQuery(id+"F2.wireOp",EDGE,"E125.sketch_text.stroke-9"),sQuery(id+"F2.wireOp",EDGE,"E125.sketch_text.stroke-10"),sQuery(id+"F2.wireOp",EDGE,"E125.sketch_text.stroke-11"),sQuery(id+"F2.wireOp",EDGE,"E125.sketch_text.stroke-12"),sQuery(id+"F2.wireOp",EDGE,"E125.sketch_text.stroke-13")])]});
            var Q1;
            Q1=makeQuery(id+"F3.opExtrude","SWEPT_BODY",BODY,{"disambiguationData":[OSD([sQuery(id+"F2.wireOp",EDGE,"E125.sketch_text.stroke-14"),sQuery(id+"F2.wireOp",EDGE,"E125.sketch_text.stroke-15"),sQuery(id+"F2.wireOp",EDGE,"E125.sketch_text.stroke-16"),sQuery(id+"F2.wireOp",EDGE,"E125.sketch_text.stroke-17")])]});
            var Q2;
            Q2=makeQuery(id+"F3.opExtrude","SWEPT_BODY",BODY,{"disambiguationData":[OSD([sQuery(id+"F2.wireOp",EDGE,"E126.sketch_text.stroke-0"),sQuery(id+"F2.wireOp",EDGE,"E126.sketch_text.stroke-1"),sQuery(id+"F2.wireOp",EDGE,"E126.sketch_text.stroke-2"),sQuery(id+"F2.wireOp",EDGE,"E126.sketch_text.stroke-3"),sQuery(id+"F2.wireOp",EDGE,"E126.sketch_text.stroke-4"),sQuery(id+"F2.wireOp",EDGE,"E126.sketch_text.stroke-5"),sQuery(id+"F2.wireOp",EDGE,"E126.sketch_text.stroke-6"),sQuery(id+"F2.wireOp",EDGE,"E126.sketch_text.stroke-7"),sQuery(id+"F2.wireOp",EDGE,"E126.sketch_text.stroke-8"),sQuery(id+"F2.wireOp",EDGE,"E126.sketch_text.stroke-9"),sQuery(id+"F2.wireOp",EDGE,"E126.sketch_text.stroke-10"),sQuery(id+"F2.wireOp",EDGE,"E126.sketch_text.stroke-11"),sQuery(id+"F2.wireOp",EDGE,"E126.sketch_text.stroke-12"),sQuery(id+"F2.wireOp",EDGE,"E126.sketch_text.stroke-13"),sQuery(id+"F2.wireOp",EDGE,"E126.sketch_text.stroke-14"),sQuery(id+"F2.wireOp",EDGE,"E126.sketch_text.stroke-15"),sQuery(id+"F2.wireOp",EDGE,"E126.sketch_text.stroke-16")])]});
            var Q3;
            Q3=makeQuery(id+"F3.opExtrude","SWEPT_BODY",BODY,{"disambiguationData":[OSD([sQuery(id+"F2.wireOp",EDGE,"E127.sketch_text.stroke-0"),sQuery(id+"F2.wireOp",EDGE,"E127.sketch_text.stroke-1"),sQuery(id+"F2.wireOp",EDGE,"E127.sketch_text.stroke-2"),sQuery(id+"F2.wireOp",EDGE,"E127.sketch_text.stroke-3"),sQuery(id+"F2.wireOp",EDGE,"E127.sketch_text.stroke-4"),sQuery(id+"F2.wireOp",EDGE,"E127.sketch_text.stroke-5"),sQuery(id+"F2.wireOp",EDGE,"E127.sketch_text.stroke-6"),sQuery(id+"F2.wireOp",EDGE,"E127.sketch_text.stroke-7"),sQuery(id+"F2.wireOp",EDGE,"E127.sketch_text.stroke-8"),sQuery(id+"F2.wireOp",EDGE,"E127.sketch_text.stroke-9"),sQuery(id+"F2.wireOp",EDGE,"E127.sketch_text.stroke-10"),sQuery(id+"F2.wireOp",EDGE,"E127.sketch_text.stroke-11"),sQuery(id+"F2.wireOp",EDGE,"E127.sketch_text.stroke-12"),sQuery(id+"F2.wireOp",EDGE,"E127.sketch_text.stroke-13"),sQuery(id+"F2.wireOp",EDGE,"E127.sketch_text.stroke-14"),sQuery(id+"F2.wireOp",EDGE,"E127.sketch_text.stroke-15")])]});
            var Q4;
            Q4=makeQuery(id+"F3.opExtrude","SWEPT_BODY",BODY,{"disambiguationData":[OSD([sQuery(id+"F2.wireOp",EDGE,"E127.sketch_text.stroke-16"),sQuery(id+"F2.wireOp",EDGE,"E127.sketch_text.stroke-17"),sQuery(id+"F2.wireOp",EDGE,"E127.sketch_text.stroke-18"),sQuery(id+"F2.wireOp",EDGE,"E127.sketch_text.stroke-19"),sQuery(id+"F2.wireOp",EDGE,"E127.sketch_text.stroke-20"),sQuery(id+"F2.wireOp",EDGE,"E127.sketch_text.stroke-21"),sQuery(id+"F2.wireOp",EDGE,"E127.sketch_text.stroke-22"),sQuery(id+"F2.wireOp",EDGE,"E127.sketch_text.stroke-23"),sQuery(id+"F2.wireOp",EDGE,"E127.sketch_text.stroke-24"),sQuery(id+"F2.wireOp",EDGE,"E127.sketch_text.stroke-25"),sQuery(id+"F2.wireOp",EDGE,"E127.sketch_text.stroke-26"),sQuery(id+"F2.wireOp",EDGE,"E127.sketch_text.stroke-27")])]});
            var Q5;
            Q5=makeQuery(id+"F3.opExtrude","SWEPT_BODY",BODY,{"disambiguationData":[OSD([sQuery(id+"F2.wireOp",EDGE,"E127.sketch_text.stroke-28"),sQuery(id+"F2.wireOp",EDGE,"E127.sketch_text.stroke-29"),sQuery(id+"F2.wireOp",EDGE,"E127.sketch_text.stroke-30"),sQuery(id+"F2.wireOp",EDGE,"E127.sketch_text.stroke-31"),sQuery(id+"F2.wireOp",EDGE,"E127.sketch_text.stroke-32"),sQuery(id+"F2.wireOp",EDGE,"E127.sketch_text.stroke-33"),sQuery(id+"F2.wireOp",EDGE,"E127.sketch_text.stroke-34"),sQuery(id+"F2.wireOp",EDGE,"E127.sketch_text.stroke-35"),sQuery(id+"F2.wireOp",EDGE,"E127.sketch_text.stroke-36"),sQuery(id+"F2.wireOp",EDGE,"E127.sketch_text.stroke-37"),sQuery(id+"F2.wireOp",EDGE,"E127.sketch_text.stroke-38"),sQuery(id+"F2.wireOp",EDGE,"E127.sketch_text.stroke-39")])]});
            var Q6;
            Q6=qCreatedBy(makeId("Origin.pointOp"),VERTEX);
            transform(context, id + "F6", {"entities" : qUnion([Q0, Q1, Q2, Q3, Q4, Q5]), "transformType" : TransformType.SCALE_UNIFORMLY, "scale" : 0.4, "scalePoint" : qUnion([Q6]), "makeCopy" : false});
        }
        {
            var Q0;
            Q0=makeQuery(id+"F3.opExtrude","SWEPT_BODY",BODY,{"disambiguationData":[OSD([sQuery(id+"F2.wireOp",EDGE,"E125.sketch_text.stroke-0"),sQuery(id+"F2.wireOp",EDGE,"E125.sketch_text.stroke-1"),sQuery(id+"F2.wireOp",EDGE,"E125.sketch_text.stroke-2"),sQuery(id+"F2.wireOp",EDGE,"E125.sketch_text.stroke-3"),sQuery(id+"F2.wireOp",EDGE,"E125.sketch_text.stroke-4"),sQuery(id+"F2.wireOp",EDGE,"E125.sketch_text.stroke-5"),sQuery(id+"F2.wireOp",EDGE,"E125.sketch_text.stroke-6"),sQuery(id+"F2.wireOp",EDGE,"E125.sketch_text.stroke-7"),sQuery(id+"F2.wireOp",EDGE,"E125.sketch_text.stroke-8"),sQuery(id+"F2.wireOp",EDGE,"E125.sketch_text.stroke-9"),sQuery(id+"F2.wireOp",EDGE,"E125.sketch_text.stroke-10"),sQuery(id+"F2.wireOp",EDGE,"E125.sketch_text.stroke-11"),sQuery(id+"F2.wireOp",EDGE,"E125.sketch_text.stroke-12"),sQuery(id+"F2.wireOp",EDGE,"E125.sketch_text.stroke-13")])]});
            var Q1;
            Q1=makeQuery(id+"F3.opExtrude","SWEPT_BODY",BODY,{"disambiguationData":[OSD([sQuery(id+"F2.wireOp",EDGE,"E125.sketch_text.stroke-14"),sQuery(id+"F2.wireOp",EDGE,"E125.sketch_text.stroke-15"),sQuery(id+"F2.wireOp",EDGE,"E125.sketch_text.stroke-16"),sQuery(id+"F2.wireOp",EDGE,"E125.sketch_text.stroke-17")])]});
            var Q2;
            Q2=makeQuery(id+"F3.opExtrude","SWEPT_BODY",BODY,{"disambiguationData":[OSD([sQuery(id+"F2.wireOp",EDGE,"E126.sketch_text.stroke-0"),sQuery(id+"F2.wireOp",EDGE,"E126.sketch_text.stroke-1"),sQuery(id+"F2.wireOp",EDGE,"E126.sketch_text.stroke-2"),sQuery(id+"F2.wireOp",EDGE,"E126.sketch_text.stroke-3"),sQuery(id+"F2.wireOp",EDGE,"E126.sketch_text.stroke-4"),sQuery(id+"F2.wireOp",EDGE,"E126.sketch_text.stroke-5"),sQuery(id+"F2.wireOp",EDGE,"E126.sketch_text.stroke-6"),sQuery(id+"F2.wireOp",EDGE,"E126.sketch_text.stroke-7"),sQuery(id+"F2.wireOp",EDGE,"E126.sketch_text.stroke-8"),sQuery(id+"F2.wireOp",EDGE,"E126.sketch_text.stroke-9"),sQuery(id+"F2.wireOp",EDGE,"E126.sketch_text.stroke-10"),sQuery(id+"F2.wireOp",EDGE,"E126.sketch_text.stroke-11"),sQuery(id+"F2.wireOp",EDGE,"E126.sketch_text.stroke-12"),sQuery(id+"F2.wireOp",EDGE,"E126.sketch_text.stroke-13"),sQuery(id+"F2.wireOp",EDGE,"E126.sketch_text.stroke-14"),sQuery(id+"F2.wireOp",EDGE,"E126.sketch_text.stroke-15"),sQuery(id+"F2.wireOp",EDGE,"E126.sketch_text.stroke-16")])]});
            var Q3;
            Q3=makeQuery(id+"F3.opExtrude","SWEPT_BODY",BODY,{"disambiguationData":[OSD([sQuery(id+"F2.wireOp",EDGE,"E127.sketch_text.stroke-0"),sQuery(id+"F2.wireOp",EDGE,"E127.sketch_text.stroke-1"),sQuery(id+"F2.wireOp",EDGE,"E127.sketch_text.stroke-2"),sQuery(id+"F2.wireOp",EDGE,"E127.sketch_text.stroke-3"),sQuery(id+"F2.wireOp",EDGE,"E127.sketch_text.stroke-4"),sQuery(id+"F2.wireOp",EDGE,"E127.sketch_text.stroke-5"),sQuery(id+"F2.wireOp",EDGE,"E127.sketch_text.stroke-6"),sQuery(id+"F2.wireOp",EDGE,"E127.sketch_text.stroke-7"),sQuery(id+"F2.wireOp",EDGE,"E127.sketch_text.stroke-8"),sQuery(id+"F2.wireOp",EDGE,"E127.sketch_text.stroke-9"),sQuery(id+"F2.wireOp",EDGE,"E127.sketch_text.stroke-10"),sQuery(id+"F2.wireOp",EDGE,"E127.sketch_text.stroke-11"),sQuery(id+"F2.wireOp",EDGE,"E127.sketch_text.stroke-12"),sQuery(id+"F2.wireOp",EDGE,"E127.sketch_text.stroke-13"),sQuery(id+"F2.wireOp",EDGE,"E127.sketch_text.stroke-14"),sQuery(id+"F2.wireOp",EDGE,"E127.sketch_text.stroke-15")])]});
            var Q4;
            Q4=makeQuery(id+"F3.opExtrude","SWEPT_BODY",BODY,{"disambiguationData":[OSD([sQuery(id+"F2.wireOp",EDGE,"E127.sketch_text.stroke-16"),sQuery(id+"F2.wireOp",EDGE,"E127.sketch_text.stroke-17"),sQuery(id+"F2.wireOp",EDGE,"E127.sketch_text.stroke-18"),sQuery(id+"F2.wireOp",EDGE,"E127.sketch_text.stroke-19"),sQuery(id+"F2.wireOp",EDGE,"E127.sketch_text.stroke-20"),sQuery(id+"F2.wireOp",EDGE,"E127.sketch_text.stroke-21"),sQuery(id+"F2.wireOp",EDGE,"E127.sketch_text.stroke-22"),sQuery(id+"F2.wireOp",EDGE,"E127.sketch_text.stroke-23"),sQuery(id+"F2.wireOp",EDGE,"E127.sketch_text.stroke-24"),sQuery(id+"F2.wireOp",EDGE,"E127.sketch_text.stroke-25"),sQuery(id+"F2.wireOp",EDGE,"E127.sketch_text.stroke-26"),sQuery(id+"F2.wireOp",EDGE,"E127.sketch_text.stroke-27")])]});
            var Q5;
            Q5=makeQuery(id+"F3.opExtrude","SWEPT_BODY",BODY,{"disambiguationData":[OSD([sQuery(id+"F2.wireOp",EDGE,"E127.sketch_text.stroke-28"),sQuery(id+"F2.wireOp",EDGE,"E127.sketch_text.stroke-29"),sQuery(id+"F2.wireOp",EDGE,"E127.sketch_text.stroke-30"),sQuery(id+"F2.wireOp",EDGE,"E127.sketch_text.stroke-31"),sQuery(id+"F2.wireOp",EDGE,"E127.sketch_text.stroke-32"),sQuery(id+"F2.wireOp",EDGE,"E127.sketch_text.stroke-33"),sQuery(id+"F2.wireOp",EDGE,"E127.sketch_text.stroke-34"),sQuery(id+"F2.wireOp",EDGE,"E127.sketch_text.stroke-35"),sQuery(id+"F2.wireOp",EDGE,"E127.sketch_text.stroke-36"),sQuery(id+"F2.wireOp",EDGE,"E127.sketch_text.stroke-37"),sQuery(id+"F2.wireOp",EDGE,"E127.sketch_text.stroke-38"),sQuery(id+"F2.wireOp",EDGE,"E127.sketch_text.stroke-39")])]});
            transform(context, id + "F7", {"entities" : qUnion([Q0, Q1, Q2, Q3, Q4, Q5]), "transformType" : TransformType.TRANSLATION_3D, "dx" : 37.3 * mm, "dy" : -12.3 * mm, "dz" : 0 * mm, "makeCopy" : false});
        }
        {
            var Q0;
            Q0=qCreatedBy(makeId("Top.planeOp"),FACE);
            var sketch = newSketch(context, id + "F8", { "sketchPlane" : qUnion([Q0])});
            skLineSegment(sketch, "E128.bottom", {"start": v(-103.71, -22.6) * mm, "end": v(99.76, -22.6) * mm});
            skLineSegment(sketch, "E128.top", {"start": v(-103.71, 39.05) * mm, "end": v(99.76, 39.05) * mm});
            skLineSegment(sketch, "E128.left", {"start": v(-103.71, -22.6) * mm, "end": v(-103.71, 39.05) * mm});
            skLineSegment(sketch, "E128.right", {"start": v(99.76, -22.6) * mm, "end": v(99.76, 39.05) * mm});
            skSolve(sketch);
        }
        {
            var Q0;
            Q0=makeQuery(id+"F8.imprint","IMPRINT",FACE,{"disambiguationData":[TD([[makeQuery(id+"F8.imprint","IMPRINT",EDGE,{"derivedFrom":sQuery(id+"F8.wireOp",EDGE,"E128.bottom")}),1.0]])]});
            extrude(context, id + "F9", {"entities" : qUnion([Q0]), "depth" : 5 * mm, "offsetDistance" : 25 * mm});
        }
        {
            var Q0;
            Q0=qCreatedBy(makeId("Top.planeOp"),FACE);
            var sketch = newSketch(context, id + "F10", { "sketchPlane" : qUnion([Q0])});
            skCircle(sketch, "E129", {"center": v(-68.08, -5.06) * mm, "radius": 3 * mm});
            skCircle(sketch, "E130", {"center": v(-94.17, 4.87) * mm, "radius": 3 * mm});
            skCircle(sketch, "E131", {"center": v(-49.72, -5.12) * mm, "radius": 3 * mm});
            skCircle(sketch, "E132", {"center": v(-49.47, 11.51) * mm, "radius": 3 * mm});
            skCircle(sketch, "E133", {"center": v(-34.14, 3) * mm, "radius": 3 * mm});
            skCircle(sketch, "E134", {"center": v(-13.3, -5.22) * mm, "radius": 3 * mm});
            skCircle(sketch, "E135", {"center": v(-13.47, 11.6) * mm, "radius": 3 * mm});
            skCircle(sketch, "E136", {"center": v(0, -5.26) * mm, "radius": 3 * mm});
            skCircle(sketch, "E137", {"center": v(0, 11.64) * mm, "radius": 3 * mm});
            skCircle(sketch, "E138", {"center": v(15.9, 2.94) * mm, "radius": 3 * mm});
            skCircle(sketch, "E139", {"center": v(55.97, -5.42) * mm, "radius": 3 * mm});
            skCircle(sketch, "E140", {"center": v(55.5, 11.78) * mm, "radius": 3 * mm});
            skCircle(sketch, "E141", {"center": v(37.05, 2.92) * mm, "radius": 3 * mm});
            skCircle(sketch, "E142", {"center": v(70.61, 11.82) * mm, "radius": 3 * mm});
            skCircle(sketch, "E143", {"center": v(90.2, -5.52) * mm, "radius": 3 * mm});
            skCircle(sketch, "E144", {"center": v(39.46, 25.28) * mm, "radius": 3 * mm});
            skCircle(sketch, "E145", {"center": v(63.42, 25.22) * mm, "radius": 3 * mm});
            skCircle(sketch, "E146", {"center": v(-9.03, 25.39) * mm, "radius": 3 * mm});
            skCircle(sketch, "E147", {"center": v(3.87, 25.36) * mm, "radius": 3 * mm});
            skCircle(sketch, "E148", {"center": v(-17.88, 25.4) * mm, "radius": 3 * mm});
            skCircle(sketch, "E149", {"center": v(-26.98, 25.43) * mm, "radius": 3 * mm});
            skCircle(sketch, "E150", {"center": v(-48.23, 25.48) * mm, "radius": 3 * mm});
            skCircle(sketch, "E151", {"center": v(-70.11, 25.53) * mm, "radius": 3 * mm});
            skCircle(sketch, "E152", {"center": v(-94.17, 4.87) * mm, "radius": 2 * mm});
            skCircle(sketch, "E153", {"center": v(-68.08, -5.06) * mm, "radius": 2 * mm});
            skCircle(sketch, "E154", {"center": v(-49.72, -5.12) * mm, "radius": 2 * mm});
            skCircle(sketch, "E155", {"center": v(-49.47, 11.51) * mm, "radius": 2 * mm});
            skCircle(sketch, "E156", {"center": v(-34.14, 3) * mm, "radius": 2 * mm});
            skCircle(sketch, "E157", {"center": v(-13.3, -5.22) * mm, "radius": 2 * mm});
            skCircle(sketch, "E158", {"center": v(-13.47, 11.6) * mm, "radius": 2 * mm});
            skCircle(sketch, "E159", {"center": v(0, 11.64) * mm, "radius": 2 * mm});
            skCircle(sketch, "E160", {"center": v(0, -5.26) * mm, "radius": 2 * mm});
            skCircle(sketch, "E161", {"center": v(15.9, 2.94) * mm, "radius": 2 * mm});
            skCircle(sketch, "E162", {"center": v(37.05, 2.92) * mm, "radius": 2 * mm});
            skCircle(sketch, "E163", {"center": v(55.97, -5.42) * mm, "radius": 2 * mm});
            skCircle(sketch, "E164", {"center": v(55.5, 11.78) * mm, "radius": 2 * mm});
            skCircle(sketch, "E165", {"center": v(70.61, 11.82) * mm, "radius": 2 * mm});
            skCircle(sketch, "E166", {"center": v(90.2, -5.52) * mm, "radius": 2 * mm});
            skCircle(sketch, "E167", {"center": v(63.42, 25.22) * mm, "radius": 2 * mm});
            skCircle(sketch, "E168", {"center": v(39.46, 25.28) * mm, "radius": 2 * mm});
            skCircle(sketch, "E169", {"center": v(3.87, 25.36) * mm, "radius": 2 * mm});
            skCircle(sketch, "E170", {"center": v(-9.03, 25.39) * mm, "radius": 2 * mm});
            skCircle(sketch, "E171", {"center": v(-17.88, 25.4) * mm, "radius": 2 * mm});
            skCircle(sketch, "E172", {"center": v(-26.98, 25.43) * mm, "radius": 2 * mm});
            skCircle(sketch, "E173", {"center": v(-48.23, 25.48) * mm, "radius": 2 * mm});
            skCircle(sketch, "E174", {"center": v(-70.11, 25.53) * mm, "radius": 2 * mm});
            skLineSegment(sketch, "E175", {"start": v(-68.08, -5.06) * mm, "end": v(-49.72, -5.12) * mm, "construction": true});
            skLineSegment(sketch, "E176", {"start": v(-49.72, -5.12) * mm, "end": v(-13.3, -5.22) * mm, "construction": true});
            skLineSegment(sketch, "E177", {"start": v(-13.3, -5.22) * mm, "end": v(0, -5.26) * mm, "construction": true});
            skLineSegment(sketch, "E178", {"start": v(0, -5.26) * mm, "end": v(55.97, -5.42) * mm, "construction": true});
            skLineSegment(sketch, "E179", {"start": v(55.97, -5.42) * mm, "end": v(90.2, -5.52) * mm, "construction": true});
            skLineSegment(sketch, "E180", {"start": v(-34.14, 3) * mm, "end": v(15.9, 2.94) * mm, "construction": true});
            skLineSegment(sketch, "E181", {"start": v(15.9, 2.94) * mm, "end": v(37.05, 2.92) * mm, "construction": true});
            skLineSegment(sketch, "E182", {"start": v(-49.47, 11.51) * mm, "end": v(-13.47, 11.6) * mm, "construction": true});
            skLineSegment(sketch, "E183", {"start": v(-13.47, 11.6) * mm, "end": v(0, 11.64) * mm, "construction": true});
            skLineSegment(sketch, "E184", {"start": v(0, 11.64) * mm, "end": v(55.5, 11.78) * mm, "construction": true});
            skLineSegment(sketch, "E185", {"start": v(55.5, 11.78) * mm, "end": v(70.61, 11.82) * mm, "construction": true});
            skLineSegment(sketch, "E186", {"start": v(-70.11, 25.53) * mm, "end": v(-48.23, 25.48) * mm, "construction": true});
            skLineSegment(sketch, "E187", {"start": v(-48.23, 25.48) * mm, "end": v(-26.98, 25.43) * mm, "construction": true});
            skLineSegment(sketch, "E188", {"start": v(-26.98, 25.43) * mm, "end": v(-17.88, 25.4) * mm, "construction": true});
            skLineSegment(sketch, "E189", {"start": v(-17.88, 25.4) * mm, "end": v(-9.03, 25.39) * mm, "construction": true});
            skLineSegment(sketch, "E190", {"start": v(-9.03, 25.39) * mm, "end": v(3.87, 25.36) * mm, "construction": true});
            skLineSegment(sketch, "E191", {"start": v(3.87, 25.36) * mm, "end": v(39.46, 25.28) * mm, "construction": true});
            skLineSegment(sketch, "E192", {"start": v(39.46, 25.28) * mm, "end": v(63.42, 25.22) * mm, "construction": true});
            skSolve(sketch);
        }
        {
            var Q0;
            Q0=makeQuery(id+"F10.imprint","IMPRINT",FACE,{"disambiguationData":[TD([[makeQuery(id+"F10.imprint","IMPRINT",EDGE,{"derivedFrom":sQuery(id+"F10.wireOp",EDGE,"E129")}),1.0]])]});
            var Q1;
            Q1=makeQuery(id+"F10.imprint","IMPRINT",FACE,{"disambiguationData":[TD([[makeQuery(id+"F10.imprint","IMPRINT",EDGE,{"derivedFrom":sQuery(id+"F10.wireOp",EDGE,"E131")}),1.0]])]});
            var Q2;
            Q2=makeQuery(id+"F10.imprint","IMPRINT",FACE,{"disambiguationData":[TD([[makeQuery(id+"F10.imprint","IMPRINT",EDGE,{"derivedFrom":sQuery(id+"F10.wireOp",EDGE,"E130")}),1.0]])]});
            var Q3;
            Q3=makeQuery(id+"F10.imprint","IMPRINT",FACE,{"disambiguationData":[TD([[makeQuery(id+"F10.imprint","IMPRINT",EDGE,{"derivedFrom":sQuery(id+"F10.wireOp",EDGE,"E132")}),1.0]])]});
            var Q4;
            Q4=makeQuery(id+"F10.imprint","IMPRINT",FACE,{"disambiguationData":[TD([[makeQuery(id+"F10.imprint","IMPRINT",EDGE,{"derivedFrom":sQuery(id+"F10.wireOp",EDGE,"E133")}),1.0]])]});
            var Q5;
            Q5=makeQuery(id+"F10.imprint","IMPRINT",FACE,{"disambiguationData":[TD([[makeQuery(id+"F10.imprint","IMPRINT",EDGE,{"derivedFrom":sQuery(id+"F10.wireOp",EDGE,"E134")}),1.0]])]});
            var Q6;
            Q6=makeQuery(id+"F10.imprint","IMPRINT",FACE,{"disambiguationData":[TD([[makeQuery(id+"F10.imprint","IMPRINT",EDGE,{"derivedFrom":sQuery(id+"F10.wireOp",EDGE,"E136")}),1.0]])]});
            var Q7;
            Q7=makeQuery(id+"F10.imprint","IMPRINT",FACE,{"disambiguationData":[TD([[makeQuery(id+"F10.imprint","IMPRINT",EDGE,{"derivedFrom":sQuery(id+"F10.wireOp",EDGE,"E138")}),1.0]])]});
            var Q8;
            Q8=makeQuery(id+"F10.imprint","IMPRINT",FACE,{"disambiguationData":[TD([[makeQuery(id+"F10.imprint","IMPRINT",EDGE,{"derivedFrom":sQuery(id+"F10.wireOp",EDGE,"E141")}),1.0]])]});
            var Q9;
            Q9=makeQuery(id+"F10.imprint","IMPRINT",FACE,{"disambiguationData":[TD([[makeQuery(id+"F10.imprint","IMPRINT",EDGE,{"derivedFrom":sQuery(id+"F10.wireOp",EDGE,"E139")}),1.0]])]});
            var Q10;
            Q10=makeQuery(id+"F10.imprint","IMPRINT",FACE,{"disambiguationData":[TD([[makeQuery(id+"F10.imprint","IMPRINT",EDGE,{"derivedFrom":sQuery(id+"F10.wireOp",EDGE,"E140")}),1.0]])]});
            var Q11;
            Q11=makeQuery(id+"F10.imprint","IMPRINT",FACE,{"disambiguationData":[TD([[makeQuery(id+"F10.imprint","IMPRINT",EDGE,{"derivedFrom":sQuery(id+"F10.wireOp",EDGE,"E142")}),1.0]])]});
            var Q12;
            Q12=makeQuery(id+"F10.imprint","IMPRINT",FACE,{"disambiguationData":[TD([[makeQuery(id+"F10.imprint","IMPRINT",EDGE,{"derivedFrom":sQuery(id+"F10.wireOp",EDGE,"E143")}),1.0]])]});
            var Q13;
            Q13=makeQuery(id+"F10.imprint","IMPRINT",FACE,{"disambiguationData":[TD([[makeQuery(id+"F10.imprint","IMPRINT",EDGE,{"derivedFrom":sQuery(id+"F10.wireOp",EDGE,"E137")}),1.0]])]});
            var Q14;
            Q14=makeQuery(id+"F10.imprint","IMPRINT",FACE,{"disambiguationData":[TD([[makeQuery(id+"F10.imprint","IMPRINT",EDGE,{"derivedFrom":sQuery(id+"F10.wireOp",EDGE,"E135")}),1.0]])]});
            var Q15;
            Q15=makeQuery(id+"F10.imprint","IMPRINT",FACE,{"disambiguationData":[TD([[makeQuery(id+"F10.imprint","IMPRINT",EDGE,{"derivedFrom":sQuery(id+"F10.wireOp",EDGE,"E150")}),1.0]])]});
            var Q16;
            Q16=makeQuery(id+"F10.imprint","IMPRINT",FACE,{"disambiguationData":[TD([[makeQuery(id+"F10.imprint","IMPRINT",EDGE,{"derivedFrom":sQuery(id+"F10.wireOp",EDGE,"E149")}),1.0]])]});
            var Q17;
            Q17=makeQuery(id+"F10.imprint","IMPRINT",FACE,{"disambiguationData":[TD([[makeQuery(id+"F10.imprint","IMPRINT",EDGE,{"derivedFrom":sQuery(id+"F10.wireOp",EDGE,"E148")}),1.0]])]});
            var Q18;
            Q18=makeQuery(id+"F10.imprint","IMPRINT",FACE,{"disambiguationData":[TD([[makeQuery(id+"F10.imprint","IMPRINT",EDGE,{"derivedFrom":sQuery(id+"F10.wireOp",EDGE,"E146")}),1.0]])]});
            var Q19;
            Q19=makeQuery(id+"F10.imprint","IMPRINT",FACE,{"disambiguationData":[TD([[makeQuery(id+"F10.imprint","IMPRINT",EDGE,{"derivedFrom":sQuery(id+"F10.wireOp",EDGE,"E147")}),1.0]])]});
            var Q20;
            Q20=makeQuery(id+"F10.imprint","IMPRINT",FACE,{"disambiguationData":[TD([[makeQuery(id+"F10.imprint","IMPRINT",EDGE,{"derivedFrom":sQuery(id+"F10.wireOp",EDGE,"E145")}),1.0]])]});
            var Q21;
            Q21=makeQuery(id+"F10.imprint","IMPRINT",FACE,{"disambiguationData":[TD([[makeQuery(id+"F10.imprint","IMPRINT",EDGE,{"derivedFrom":sQuery(id+"F10.wireOp",EDGE,"E151")}),1.0]])]});
            var Q22;
            Q22=makeQuery(id+"F10.imprint","IMPRINT",FACE,{"disambiguationData":[TD([[makeQuery(id+"F10.imprint","IMPRINT",EDGE,{"derivedFrom":sQuery(id+"F10.wireOp",EDGE,"E144")}),1.0]])]});
            extrude(context, id + "F11", {"entities" : qUnion([Q0, Q1, Q2, Q3, Q4, Q5, Q6, Q7, Q8, Q9, Q10, Q11, Q12, Q13, Q14, Q15, Q16, Q17, Q18, Q19, Q20, Q21, Q22]), "operationType" : NewBodyOperationType.REMOVE, "depth" : 4 * mm, "offsetDistance" : 25 * mm});
        }
        {
            var Q0;
            Q0=makeQuery(id+"F11.boolean.opBoolean","SPLIT",FACE,{"disambiguationData":[TD([makeQuery(id+"F11.opExtrude","SWEPT_FACE",FACE,{"disambiguationData":[OSD([sQuery(id+"F10.wireOp",EDGE,"E152")])]})])],"derivedFrom":makeQuery(id+"F9.opExtrude","CAP_FACE",FACE,{"disambiguationData":[OSD([sQuery(id+"F8.wireOp",EDGE,"E128.bottom"),sQuery(id+"F8.wireOp",EDGE,"E128.top"),sQuery(id+"F8.wireOp",EDGE,"E128.left"),sQuery(id+"F8.wireOp",EDGE,"E128.right")])],"isStart":true})});
            var Q1;
            Q1=makeQuery(id+"F11.boolean.opBoolean","SPLIT",FACE,{"disambiguationData":[TD([makeQuery(id+"F11.opExtrude","SWEPT_FACE",FACE,{"disambiguationData":[OSD([sQuery(id+"F10.wireOp",EDGE,"E153")])]})])],"derivedFrom":makeQuery(id+"F9.opExtrude","CAP_FACE",FACE,{"disambiguationData":[OSD([sQuery(id+"F8.wireOp",EDGE,"E128.bottom"),sQuery(id+"F8.wireOp",EDGE,"E128.top"),sQuery(id+"F8.wireOp",EDGE,"E128.left"),sQuery(id+"F8.wireOp",EDGE,"E128.right")])],"isStart":true})});
            var Q2;
            Q2=makeQuery(id+"F11.boolean.opBoolean","SPLIT",FACE,{"disambiguationData":[TD([makeQuery(id+"F11.opExtrude","SWEPT_FACE",FACE,{"disambiguationData":[OSD([sQuery(id+"F10.wireOp",EDGE,"E154")])]})])],"derivedFrom":makeQuery(id+"F9.opExtrude","CAP_FACE",FACE,{"disambiguationData":[OSD([sQuery(id+"F8.wireOp",EDGE,"E128.bottom"),sQuery(id+"F8.wireOp",EDGE,"E128.top"),sQuery(id+"F8.wireOp",EDGE,"E128.left"),sQuery(id+"F8.wireOp",EDGE,"E128.right")])],"isStart":true})});
            var Q3;
            Q3=makeQuery(id+"F11.boolean.opBoolean","SPLIT",FACE,{"disambiguationData":[TD([makeQuery(id+"F11.opExtrude","SWEPT_FACE",FACE,{"disambiguationData":[OSD([sQuery(id+"F10.wireOp",EDGE,"E155")])]})])],"derivedFrom":makeQuery(id+"F9.opExtrude","CAP_FACE",FACE,{"disambiguationData":[OSD([sQuery(id+"F8.wireOp",EDGE,"E128.bottom"),sQuery(id+"F8.wireOp",EDGE,"E128.top"),sQuery(id+"F8.wireOp",EDGE,"E128.left"),sQuery(id+"F8.wireOp",EDGE,"E128.right")])],"isStart":true})});
            var Q4;
            Q4=makeQuery(id+"F11.boolean.opBoolean","SPLIT",FACE,{"disambiguationData":[TD([makeQuery(id+"F11.opExtrude","SWEPT_FACE",FACE,{"disambiguationData":[OSD([sQuery(id+"F10.wireOp",EDGE,"E156")])]})])],"derivedFrom":makeQuery(id+"F9.opExtrude","CAP_FACE",FACE,{"disambiguationData":[OSD([sQuery(id+"F8.wireOp",EDGE,"E128.bottom"),sQuery(id+"F8.wireOp",EDGE,"E128.top"),sQuery(id+"F8.wireOp",EDGE,"E128.left"),sQuery(id+"F8.wireOp",EDGE,"E128.right")])],"isStart":true})});
            var Q5;
            Q5=makeQuery(id+"F11.boolean.opBoolean","SPLIT",FACE,{"disambiguationData":[TD([makeQuery(id+"F11.opExtrude","SWEPT_FACE",FACE,{"disambiguationData":[OSD([sQuery(id+"F10.wireOp",EDGE,"E157")])]})])],"derivedFrom":makeQuery(id+"F9.opExtrude","CAP_FACE",FACE,{"disambiguationData":[OSD([sQuery(id+"F8.wireOp",EDGE,"E128.bottom"),sQuery(id+"F8.wireOp",EDGE,"E128.top"),sQuery(id+"F8.wireOp",EDGE,"E128.left"),sQuery(id+"F8.wireOp",EDGE,"E128.right")])],"isStart":true})});
            var Q6;
            Q6=makeQuery(id+"F11.boolean.opBoolean","SPLIT",FACE,{"disambiguationData":[TD([makeQuery(id+"F11.opExtrude","SWEPT_FACE",FACE,{"disambiguationData":[OSD([sQuery(id+"F10.wireOp",EDGE,"E160")])]})])],"derivedFrom":makeQuery(id+"F9.opExtrude","CAP_FACE",FACE,{"disambiguationData":[OSD([sQuery(id+"F8.wireOp",EDGE,"E128.bottom"),sQuery(id+"F8.wireOp",EDGE,"E128.top"),sQuery(id+"F8.wireOp",EDGE,"E128.left"),sQuery(id+"F8.wireOp",EDGE,"E128.right")])],"isStart":true})});
            var Q7;
            Q7=makeQuery(id+"F11.boolean.opBoolean","SPLIT",FACE,{"disambiguationData":[TD([makeQuery(id+"F11.opExtrude","SWEPT_FACE",FACE,{"disambiguationData":[OSD([sQuery(id+"F10.wireOp",EDGE,"E158")])]})])],"derivedFrom":makeQuery(id+"F9.opExtrude","CAP_FACE",FACE,{"disambiguationData":[OSD([sQuery(id+"F8.wireOp",EDGE,"E128.bottom"),sQuery(id+"F8.wireOp",EDGE,"E128.top"),sQuery(id+"F8.wireOp",EDGE,"E128.left"),sQuery(id+"F8.wireOp",EDGE,"E128.right")])],"isStart":true})});
            var Q8;
            Q8=makeQuery(id+"F11.boolean.opBoolean","SPLIT",FACE,{"disambiguationData":[TD([makeQuery(id+"F11.opExtrude","SWEPT_FACE",FACE,{"disambiguationData":[OSD([sQuery(id+"F10.wireOp",EDGE,"E159")])]})])],"derivedFrom":makeQuery(id+"F9.opExtrude","CAP_FACE",FACE,{"disambiguationData":[OSD([sQuery(id+"F8.wireOp",EDGE,"E128.bottom"),sQuery(id+"F8.wireOp",EDGE,"E128.top"),sQuery(id+"F8.wireOp",EDGE,"E128.left"),sQuery(id+"F8.wireOp",EDGE,"E128.right")])],"isStart":true})});
            var Q9;
            Q9=makeQuery(id+"F11.boolean.opBoolean","SPLIT",FACE,{"disambiguationData":[TD([makeQuery(id+"F11.opExtrude","SWEPT_FACE",FACE,{"disambiguationData":[OSD([sQuery(id+"F10.wireOp",EDGE,"E170")])]})])],"derivedFrom":makeQuery(id+"F9.opExtrude","CAP_FACE",FACE,{"disambiguationData":[OSD([sQuery(id+"F8.wireOp",EDGE,"E128.bottom"),sQuery(id+"F8.wireOp",EDGE,"E128.top"),sQuery(id+"F8.wireOp",EDGE,"E128.left"),sQuery(id+"F8.wireOp",EDGE,"E128.right")])],"isStart":true})});
            var Q10;
            Q10=makeQuery(id+"F11.boolean.opBoolean","SPLIT",FACE,{"disambiguationData":[TD([makeQuery(id+"F11.opExtrude","SWEPT_FACE",FACE,{"disambiguationData":[OSD([sQuery(id+"F10.wireOp",EDGE,"E171")])]})])],"derivedFrom":makeQuery(id+"F9.opExtrude","CAP_FACE",FACE,{"disambiguationData":[OSD([sQuery(id+"F8.wireOp",EDGE,"E128.bottom"),sQuery(id+"F8.wireOp",EDGE,"E128.top"),sQuery(id+"F8.wireOp",EDGE,"E128.left"),sQuery(id+"F8.wireOp",EDGE,"E128.right")])],"isStart":true})});
            var Q11;
            Q11=makeQuery(id+"F11.boolean.opBoolean","SPLIT",FACE,{"disambiguationData":[TD([makeQuery(id+"F11.opExtrude","SWEPT_FACE",FACE,{"disambiguationData":[OSD([sQuery(id+"F10.wireOp",EDGE,"E172")])]})])],"derivedFrom":makeQuery(id+"F9.opExtrude","CAP_FACE",FACE,{"disambiguationData":[OSD([sQuery(id+"F8.wireOp",EDGE,"E128.bottom"),sQuery(id+"F8.wireOp",EDGE,"E128.top"),sQuery(id+"F8.wireOp",EDGE,"E128.left"),sQuery(id+"F8.wireOp",EDGE,"E128.right")])],"isStart":true})});
            var Q12;
            Q12=makeQuery(id+"F11.boolean.opBoolean","SPLIT",FACE,{"disambiguationData":[TD([makeQuery(id+"F11.opExtrude","SWEPT_FACE",FACE,{"disambiguationData":[OSD([sQuery(id+"F10.wireOp",EDGE,"E173")])]})])],"derivedFrom":makeQuery(id+"F9.opExtrude","CAP_FACE",FACE,{"disambiguationData":[OSD([sQuery(id+"F8.wireOp",EDGE,"E128.bottom"),sQuery(id+"F8.wireOp",EDGE,"E128.top"),sQuery(id+"F8.wireOp",EDGE,"E128.left"),sQuery(id+"F8.wireOp",EDGE,"E128.right")])],"isStart":true})});
            var Q13;
            Q13=makeQuery(id+"F11.boolean.opBoolean","SPLIT",FACE,{"disambiguationData":[TD([makeQuery(id+"F11.opExtrude","SWEPT_FACE",FACE,{"disambiguationData":[OSD([sQuery(id+"F10.wireOp",EDGE,"E174")])]})])],"derivedFrom":makeQuery(id+"F9.opExtrude","CAP_FACE",FACE,{"disambiguationData":[OSD([sQuery(id+"F8.wireOp",EDGE,"E128.bottom"),sQuery(id+"F8.wireOp",EDGE,"E128.top"),sQuery(id+"F8.wireOp",EDGE,"E128.left"),sQuery(id+"F8.wireOp",EDGE,"E128.right")])],"isStart":true})});
            var Q14;
            Q14=makeQuery(id+"F11.boolean.opBoolean","SPLIT",FACE,{"disambiguationData":[TD([makeQuery(id+"F11.opExtrude","SWEPT_FACE",FACE,{"disambiguationData":[OSD([sQuery(id+"F10.wireOp",EDGE,"E169")])]})])],"derivedFrom":makeQuery(id+"F9.opExtrude","CAP_FACE",FACE,{"disambiguationData":[OSD([sQuery(id+"F8.wireOp",EDGE,"E128.bottom"),sQuery(id+"F8.wireOp",EDGE,"E128.top"),sQuery(id+"F8.wireOp",EDGE,"E128.left"),sQuery(id+"F8.wireOp",EDGE,"E128.right")])],"isStart":true})});
            var Q15;
            Q15=makeQuery(id+"F11.boolean.opBoolean","SPLIT",FACE,{"disambiguationData":[TD([makeQuery(id+"F11.opExtrude","SWEPT_FACE",FACE,{"disambiguationData":[OSD([sQuery(id+"F10.wireOp",EDGE,"E168")])]})])],"derivedFrom":makeQuery(id+"F9.opExtrude","CAP_FACE",FACE,{"disambiguationData":[OSD([sQuery(id+"F8.wireOp",EDGE,"E128.bottom"),sQuery(id+"F8.wireOp",EDGE,"E128.top"),sQuery(id+"F8.wireOp",EDGE,"E128.left"),sQuery(id+"F8.wireOp",EDGE,"E128.right")])],"isStart":true})});
            var Q16;
            Q16=makeQuery(id+"F11.boolean.opBoolean","SPLIT",FACE,{"disambiguationData":[TD([makeQuery(id+"F11.opExtrude","SWEPT_FACE",FACE,{"disambiguationData":[OSD([sQuery(id+"F10.wireOp",EDGE,"E167")])]})])],"derivedFrom":makeQuery(id+"F9.opExtrude","CAP_FACE",FACE,{"disambiguationData":[OSD([sQuery(id+"F8.wireOp",EDGE,"E128.bottom"),sQuery(id+"F8.wireOp",EDGE,"E128.top"),sQuery(id+"F8.wireOp",EDGE,"E128.left"),sQuery(id+"F8.wireOp",EDGE,"E128.right")])],"isStart":true})});
            var Q17;
            Q17=makeQuery(id+"F11.boolean.opBoolean","SPLIT",FACE,{"disambiguationData":[TD([makeQuery(id+"F11.opExtrude","SWEPT_FACE",FACE,{"disambiguationData":[OSD([sQuery(id+"F10.wireOp",EDGE,"E165")])]})])],"derivedFrom":makeQuery(id+"F9.opExtrude","CAP_FACE",FACE,{"disambiguationData":[OSD([sQuery(id+"F8.wireOp",EDGE,"E128.bottom"),sQuery(id+"F8.wireOp",EDGE,"E128.top"),sQuery(id+"F8.wireOp",EDGE,"E128.left"),sQuery(id+"F8.wireOp",EDGE,"E128.right")])],"isStart":true})});
            var Q18;
            Q18=makeQuery(id+"F11.boolean.opBoolean","SPLIT",FACE,{"disambiguationData":[TD([makeQuery(id+"F11.opExtrude","SWEPT_FACE",FACE,{"disambiguationData":[OSD([sQuery(id+"F10.wireOp",EDGE,"E164")])]})])],"derivedFrom":makeQuery(id+"F9.opExtrude","CAP_FACE",FACE,{"disambiguationData":[OSD([sQuery(id+"F8.wireOp",EDGE,"E128.bottom"),sQuery(id+"F8.wireOp",EDGE,"E128.top"),sQuery(id+"F8.wireOp",EDGE,"E128.left"),sQuery(id+"F8.wireOp",EDGE,"E128.right")])],"isStart":true})});
            var Q19;
            Q19=makeQuery(id+"F11.boolean.opBoolean","SPLIT",FACE,{"disambiguationData":[TD([makeQuery(id+"F11.opExtrude","SWEPT_FACE",FACE,{"disambiguationData":[OSD([sQuery(id+"F10.wireOp",EDGE,"E163")])]})])],"derivedFrom":makeQuery(id+"F9.opExtrude","CAP_FACE",FACE,{"disambiguationData":[OSD([sQuery(id+"F8.wireOp",EDGE,"E128.bottom"),sQuery(id+"F8.wireOp",EDGE,"E128.top"),sQuery(id+"F8.wireOp",EDGE,"E128.left"),sQuery(id+"F8.wireOp",EDGE,"E128.right")])],"isStart":true})});
            var Q20;
            Q20=makeQuery(id+"F11.boolean.opBoolean","SPLIT",FACE,{"disambiguationData":[TD([makeQuery(id+"F11.opExtrude","SWEPT_FACE",FACE,{"disambiguationData":[OSD([sQuery(id+"F10.wireOp",EDGE,"E162")])]})])],"derivedFrom":makeQuery(id+"F9.opExtrude","CAP_FACE",FACE,{"disambiguationData":[OSD([sQuery(id+"F8.wireOp",EDGE,"E128.bottom"),sQuery(id+"F8.wireOp",EDGE,"E128.top"),sQuery(id+"F8.wireOp",EDGE,"E128.left"),sQuery(id+"F8.wireOp",EDGE,"E128.right")])],"isStart":true})});
            var Q21;
            Q21=makeQuery(id+"F11.boolean.opBoolean","SPLIT",FACE,{"disambiguationData":[TD([makeQuery(id+"F11.opExtrude","SWEPT_FACE",FACE,{"disambiguationData":[OSD([sQuery(id+"F10.wireOp",EDGE,"E161")])]})])],"derivedFrom":makeQuery(id+"F9.opExtrude","CAP_FACE",FACE,{"disambiguationData":[OSD([sQuery(id+"F8.wireOp",EDGE,"E128.bottom"),sQuery(id+"F8.wireOp",EDGE,"E128.top"),sQuery(id+"F8.wireOp",EDGE,"E128.left"),sQuery(id+"F8.wireOp",EDGE,"E128.right")])],"isStart":true})});
            var Q22;
            Q22=makeQuery(id+"F11.boolean.opBoolean","SPLIT",FACE,{"disambiguationData":[TD([makeQuery(id+"F11.opExtrude","SWEPT_FACE",FACE,{"disambiguationData":[OSD([sQuery(id+"F10.wireOp",EDGE,"E166")])]})])],"derivedFrom":makeQuery(id+"F9.opExtrude","CAP_FACE",FACE,{"disambiguationData":[OSD([sQuery(id+"F8.wireOp",EDGE,"E128.bottom"),sQuery(id+"F8.wireOp",EDGE,"E128.top"),sQuery(id+"F8.wireOp",EDGE,"E128.left"),sQuery(id+"F8.wireOp",EDGE,"E128.right")])],"isStart":true})});
            extrude(context, id + "F12", {"entities" : qUnion([Q0, Q1, Q2, Q3, Q4, Q5, Q6, Q7, Q8, Q9, Q10, Q11, Q12, Q13, Q14, Q15, Q16, Q17, Q18, Q19, Q20, Q21, Q22]), "operationType" : NewBodyOperationType.REMOVE, "endBound" : BoundingType.THROUGH_ALL, "oppositeDirection" : true, "depth" : 25 * mm, "offsetDistance" : 25 * mm});
        }
        {
            var Q0;
            Q0=makeQuery(id+"F9.opExtrude","SWEPT_BODY",BODY,{"disambiguationData":[OSD([sQuery(id+"F8.wireOp",EDGE,"E128.bottom"),sQuery(id+"F8.wireOp",EDGE,"E128.top"),sQuery(id+"F8.wireOp",EDGE,"E128.left"),sQuery(id+"F8.wireOp",EDGE,"E128.right")])]});
            transform(context, id + "F13", {"entities" : qUnion([Q0]), "transformType" : TransformType.TRANSLATION_3D, "dx" : 0 * mm, "dy" : 0 * mm, "dz" : -5 * mm, "makeCopy" : false});
        }
        {
            var Q0;
            Q0=makeQuery(id+"F9.opExtrude","SWEPT_BODY",BODY,{"disambiguationData":[OSD([sQuery(id+"F8.wireOp",EDGE,"E128.bottom"),sQuery(id+"F8.wireOp",EDGE,"E128.top"),sQuery(id+"F8.wireOp",EDGE,"E128.left"),sQuery(id+"F8.wireOp",EDGE,"E128.right")])]});
            var Q1;
            Q1=makeQuery(id+"F3.opExtrude","SWEPT_BODY",BODY,{"disambiguationData":[OSD([sQuery(id+"F2.wireOp",EDGE,"E126.sketch_text.stroke-0"),sQuery(id+"F2.wireOp",EDGE,"E126.sketch_text.stroke-1"),sQuery(id+"F2.wireOp",EDGE,"E126.sketch_text.stroke-2"),sQuery(id+"F2.wireOp",EDGE,"E126.sketch_text.stroke-3"),sQuery(id+"F2.wireOp",EDGE,"E126.sketch_text.stroke-4"),sQuery(id+"F2.wireOp",EDGE,"E126.sketch_text.stroke-5"),sQuery(id+"F2.wireOp",EDGE,"E126.sketch_text.stroke-6"),sQuery(id+"F2.wireOp",EDGE,"E126.sketch_text.stroke-7"),sQuery(id+"F2.wireOp",EDGE,"E126.sketch_text.stroke-8"),sQuery(id+"F2.wireOp",EDGE,"E126.sketch_text.stroke-9"),sQuery(id+"F2.wireOp",EDGE,"E126.sketch_text.stroke-10"),sQuery(id+"F2.wireOp",EDGE,"E126.sketch_text.stroke-11"),sQuery(id+"F2.wireOp",EDGE,"E126.sketch_text.stroke-12"),sQuery(id+"F2.wireOp",EDGE,"E126.sketch_text.stroke-13"),sQuery(id+"F2.wireOp",EDGE,"E126.sketch_text.stroke-14"),sQuery(id+"F2.wireOp",EDGE,"E126.sketch_text.stroke-15"),sQuery(id+"F2.wireOp",EDGE,"E126.sketch_text.stroke-16")])]});
            var Q2;
            Q2=makeQuery(id+"F3.opExtrude","SWEPT_BODY",BODY,{"disambiguationData":[OSD([sQuery(id+"F2.wireOp",EDGE,"E125.sketch_text.stroke-0"),sQuery(id+"F2.wireOp",EDGE,"E125.sketch_text.stroke-1"),sQuery(id+"F2.wireOp",EDGE,"E125.sketch_text.stroke-2"),sQuery(id+"F2.wireOp",EDGE,"E125.sketch_text.stroke-3"),sQuery(id+"F2.wireOp",EDGE,"E125.sketch_text.stroke-4"),sQuery(id+"F2.wireOp",EDGE,"E125.sketch_text.stroke-5"),sQuery(id+"F2.wireOp",EDGE,"E125.sketch_text.stroke-6"),sQuery(id+"F2.wireOp",EDGE,"E125.sketch_text.stroke-7"),sQuery(id+"F2.wireOp",EDGE,"E125.sketch_text.stroke-8"),sQuery(id+"F2.wireOp",EDGE,"E125.sketch_text.stroke-9"),sQuery(id+"F2.wireOp",EDGE,"E125.sketch_text.stroke-10"),sQuery(id+"F2.wireOp",EDGE,"E125.sketch_text.stroke-11"),sQuery(id+"F2.wireOp",EDGE,"E125.sketch_text.stroke-12"),sQuery(id+"F2.wireOp",EDGE,"E125.sketch_text.stroke-13")])]});
            booleanBodies(context, id + "F14", {"operationType" : BooleanOperationType.SUBTRACTION, "tools" : qUnion([Q0]), "targets" : qUnion([Q1, Q2]), "keepTools" : true});
        }
        {
            var Q0;
            Q0=qCreatedBy(makeId("Top.planeOp"),FACE);
            var sketch = newSketch(context, id + "F15", { "sketchPlane" : qUnion([Q0])});
            skCircle(sketch, "E193.0", {"center": v(-68.08, -5.06) * mm, "radius": 2 * mm, "construction": true});
            skCircle(sketch, "E194.0", {"center": v(-49.72, -5.12) * mm, "radius": 2 * mm, "construction": true});
            skCircle(sketch, "E195.0", {"center": v(-49.47, 11.51) * mm, "radius": 2 * mm, "construction": true});
            skCircle(sketch, "E196.0", {"center": v(-48.23, 25.48) * mm, "radius": 2 * mm, "construction": true});
            skCircle(sketch, "E197.0", {"center": v(-34.14, 3) * mm, "radius": 2 * mm, "construction": true});
            skCircle(sketch, "E198.0", {"center": v(-70.11, 25.53) * mm, "radius": 2 * mm, "construction": true});
            skCircle(sketch, "E199.0", {"center": v(-94.17, 4.87) * mm, "radius": 2 * mm, "construction": true});
            skCircle(sketch, "E200.0", {"center": v(-26.98, 25.43) * mm, "radius": 2 * mm, "construction": true});
            skCircle(sketch, "E201.0", {"center": v(-17.88, 25.4) * mm, "radius": 2 * mm, "construction": true});
            skCircle(sketch, "E202.0", {"center": v(-9.03, 25.39) * mm, "radius": 2 * mm, "construction": true});
            skCircle(sketch, "E203.0", {"center": v(3.87, 25.36) * mm, "radius": 2 * mm, "construction": true});
            skCircle(sketch, "E204.0", {"center": v(0, 11.64) * mm, "radius": 2 * mm, "construction": true});
            skCircle(sketch, "E205.0", {"center": v(-13.47, 11.6) * mm, "radius": 2 * mm, "construction": true});
            skCircle(sketch, "E206.0", {"center": v(-13.3, -5.22) * mm, "radius": 2 * mm, "construction": true});
            skCircle(sketch, "E207.0", {"center": v(0, -5.26) * mm, "radius": 2 * mm, "construction": true});
            skCircle(sketch, "E208.0", {"center": v(15.9, 2.94) * mm, "radius": 2 * mm, "construction": true});
            skCircle(sketch, "E209.0", {"center": v(37.05, 2.92) * mm, "radius": 2 * mm, "construction": true});
            skCircle(sketch, "E210.0", {"center": v(39.46, 25.28) * mm, "radius": 2 * mm, "construction": true});
            skCircle(sketch, "E211.0", {"center": v(55.5, 11.78) * mm, "radius": 2 * mm, "construction": true});
            skCircle(sketch, "E212.0", {"center": v(55.97, -5.42) * mm, "radius": 2 * mm, "construction": true});
            skCircle(sketch, "E213.0", {"center": v(70.61, 11.82) * mm, "radius": 2 * mm, "construction": true});
            skCircle(sketch, "E214.0", {"center": v(63.42, 25.22) * mm, "radius": 2 * mm, "construction": true});
            skCircle(sketch, "E215.0", {"center": v(90.2, -5.52) * mm, "radius": 2 * mm, "construction": true});
            skCircle(sketch, "E216", {"center": v(-49.72, -5.12) * mm, "radius": 1.4 * mm});
            skCircle(sketch, "E217", {"center": v(-49.47, 11.51) * mm, "radius": 1.4 * mm});
            skCircle(sketch, "E218", {"center": v(-34.14, 3) * mm, "radius": 1.4 * mm});
            skCircle(sketch, "E219", {"center": v(-13.3, -5.22) * mm, "radius": 1.4 * mm});
            skCircle(sketch, "E220", {"center": v(-13.47, 11.6) * mm, "radius": 1.4 * mm});
            skCircle(sketch, "E221", {"center": v(0, 11.64) * mm, "radius": 1.4 * mm});
            skCircle(sketch, "E222", {"center": v(0, -5.26) * mm, "radius": 1.4 * mm});
            skCircle(sketch, "E223", {"center": v(-68.08, -5.06) * mm, "radius": 1.4 * mm});
            skCircle(sketch, "E224", {"center": v(-70.11, 25.53) * mm, "radius": 1.4 * mm});
            skCircle(sketch, "E225", {"center": v(-48.23, 25.48) * mm, "radius": 1.4 * mm});
            skCircle(sketch, "E226", {"center": v(-26.98, 25.43) * mm, "radius": 1.4 * mm});
            skCircle(sketch, "E227", {"center": v(-17.88, 25.4) * mm, "radius": 1.4 * mm});
            skCircle(sketch, "E228", {"center": v(-9.03, 25.39) * mm, "radius": 1.4 * mm});
            skCircle(sketch, "E229", {"center": v(3.87, 25.36) * mm, "radius": 1.4 * mm});
            skCircle(sketch, "E230", {"center": v(-94.17, 4.87) * mm, "radius": 1.4 * mm});
            skCircle(sketch, "E231", {"center": v(15.9, 2.94) * mm, "radius": 1.4 * mm});
            skCircle(sketch, "E232", {"center": v(37.05, 2.92) * mm, "radius": 1.4 * mm});
            skCircle(sketch, "E233", {"center": v(55.5, 11.78) * mm, "radius": 1.4 * mm});
            skCircle(sketch, "E234", {"center": v(55.97, -5.42) * mm, "radius": 1.4 * mm});
            skCircle(sketch, "E235", {"center": v(39.46, 25.28) * mm, "radius": 1.4 * mm});
            skCircle(sketch, "E236", {"center": v(63.42, 25.22) * mm, "radius": 1.4 * mm});
            skCircle(sketch, "E237", {"center": v(70.61, 11.82) * mm, "radius": 1.4 * mm});
            skCircle(sketch, "E238", {"center": v(90.2, -5.52) * mm, "radius": 1.4 * mm});
            skSolve(sketch);
        }
        {
            var Q0;
            Q0=makeQuery(id+"F10.imprint","IMPRINT",FACE,{"disambiguationData":[TD([[makeQuery(id+"F10.imprint","IMPRINT",EDGE,{"derivedFrom":sQuery(id+"F10.wireOp",EDGE,"E174")}),1.0]])]});
            var Q1;
            Q1=makeQuery(id+"F10.imprint","IMPRINT",FACE,{"disambiguationData":[TD([[makeQuery(id+"F10.imprint","IMPRINT",EDGE,{"derivedFrom":sQuery(id+"F10.wireOp",EDGE,"E168")}),1.0]])]});
            extrude(context, id + "F16", {"entities" : qUnion([Q0, Q1]), "operationType" : NewBodyOperationType.REMOVE, "oppositeDirection" : true, "depth" : 25 * mm, "offsetDistance" : 25 * mm});
        }
        {
            var Q0;
            Q0=makeQuery(id+"F9.opExtrude","SWEPT_EDGE",EDGE,{"disambiguationData":[OSD([sQuery(id+"F8.wireOp",EDGE,"E128.bottom"),sQuery(id+"F8.wireOp",EDGE,"E128.left")])]});
            var Q1;
            Q1=makeQuery(id+"F9.opExtrude","SWEPT_EDGE",EDGE,{"disambiguationData":[OSD([sQuery(id+"F8.wireOp",EDGE,"E128.bottom"),sQuery(id+"F8.wireOp",EDGE,"E128.right")])]});
            var Q2;
            Q2=makeQuery(id+"F9.opExtrude","SWEPT_EDGE",EDGE,{"disambiguationData":[OSD([sQuery(id+"F8.wireOp",EDGE,"E128.top"),sQuery(id+"F8.wireOp",EDGE,"E128.right")])]});
            var Q3;
            Q3=makeQuery(id+"F9.opExtrude","SWEPT_EDGE",EDGE,{"disambiguationData":[OSD([sQuery(id+"F8.wireOp",EDGE,"E128.top"),sQuery(id+"F8.wireOp",EDGE,"E128.left")])]});
            fillet(context, id + "F17", {"entities" : qUnion([Q0, Q1, Q2, Q3]), "radius" : 10 * mm, "tangentPropagation" : true, "allowEdgeOverflow" : false});
        }
    });
